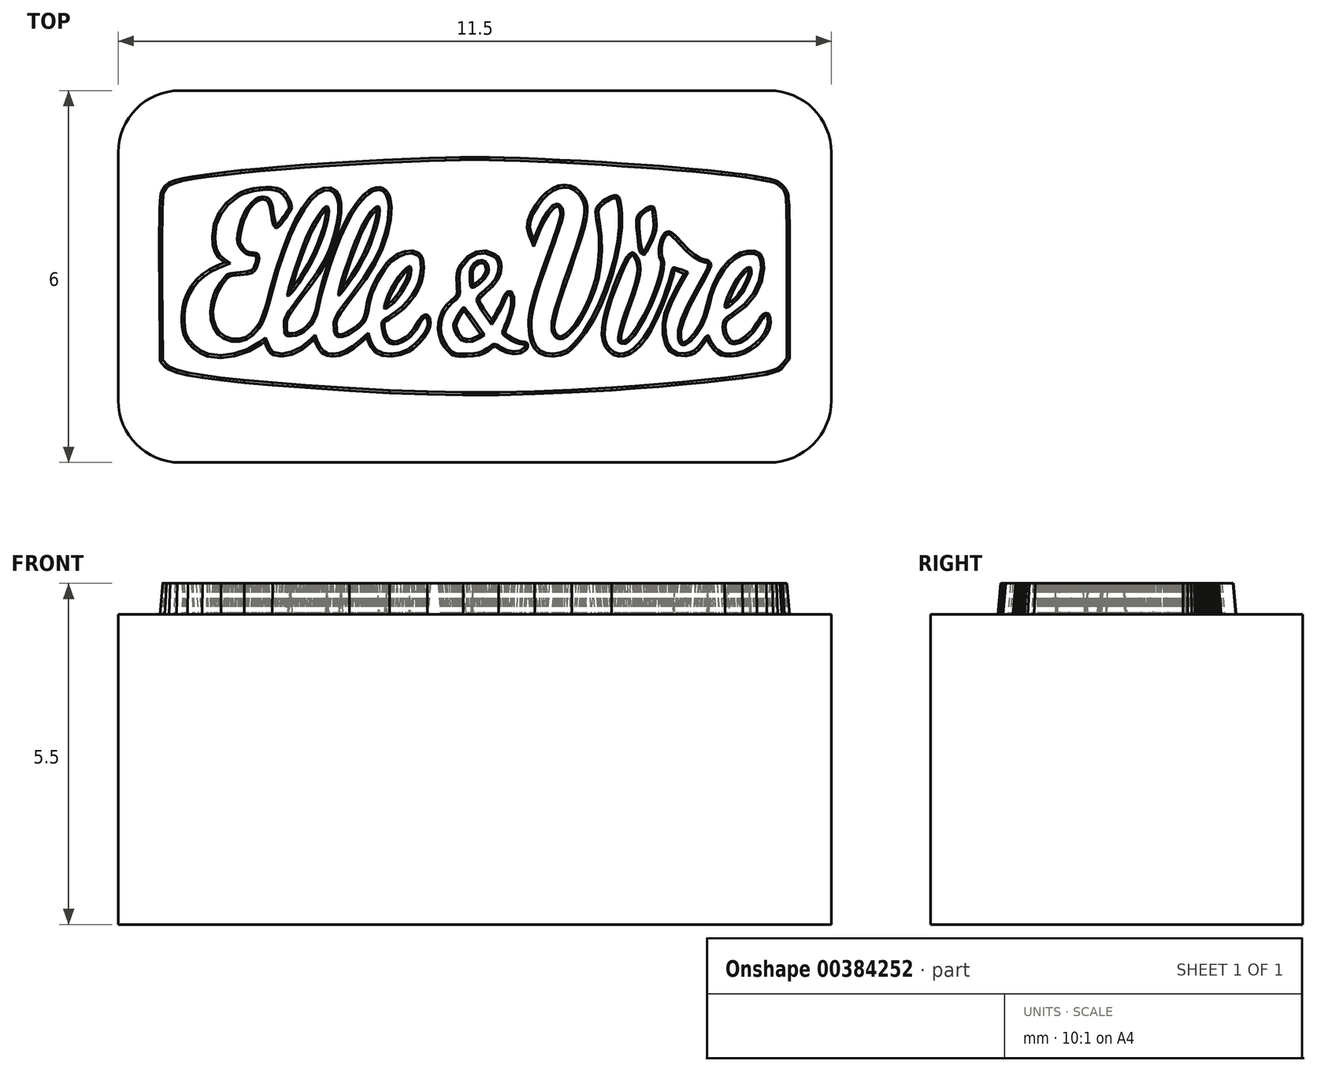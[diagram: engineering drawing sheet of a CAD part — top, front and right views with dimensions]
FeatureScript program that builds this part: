
annotation { "Feature Type Name" : "Feature", "Feature Type Description" : "" }
export const myFeature = defineFeature(function(context is Context, id is Id, definition is map)
    precondition{}
    {
        {
            var Q0;
            Q0=qCreatedBy(makeId("Top.planeOp"),FACE);
            var sketch = newSketch(context, id + "F0", { "sketchPlane" : qUnion([Q0])});
            skLineSegment(sketch, "E0.bottom", {"start": v(-4.75, 3) * mm, "end": v(4.75, 3) * mm});
            skLineSegment(sketch, "E0.top", {"start": v(-4.75, -3) * mm, "end": v(4.75, -3) * mm});
            skLineSegment(sketch, "E0.left", {"start": v(-5.75, 2) * mm, "end": v(-5.75, -2) * mm});
            skLineSegment(sketch, "E0.right", {"start": v(5.75, 2) * mm, "end": v(5.75, -2) * mm});
            skLineSegment(sketch, "E1", {"start": v(-5.75, 0) * mm, "end": v(5.75, 0) * mm});
            skPoint(sketch, "E2.visualSharp", {"position": v(-5.75, 3) * mm});
            skArc(sketch, "E2.filletArc", {"start": v(-4.75, 3) * mm, "mid": v(-5.46, 2.7) * mm, "end": v(-5.75, 2) * mm});
            skPoint(sketch, "E3.visualSharp", {"position": v(-5.75, -3) * mm});
            skArc(sketch, "E3.filletArc", {"start": v(-5.75, -2) * mm, "mid": v(-5.46, -2.7) * mm, "end": v(-4.75, -3) * mm});
            skPoint(sketch, "E4.visualSharp", {"position": v(5.75, 3) * mm});
            skArc(sketch, "E4.filletArc", {"start": v(5.75, 2) * mm, "mid": v(5.46, 2.7) * mm, "end": v(4.75, 3) * mm});
            skPoint(sketch, "E5.visualSharp", {"position": v(5.75, -3) * mm});
            skArc(sketch, "E5.filletArc", {"start": v(4.75, -3) * mm, "mid": v(5.46, -2.7) * mm, "end": v(5.75, -2) * mm});
            skSolve(sketch);
        }
        {
            var Q0;
            Q0=qCreatedBy(makeId("Top.planeOp"),FACE);
            var sketch = newSketch(context, id + "F1", { "sketchPlane" : qUnion([Q0])});
            skLineSegment(sketch, "E6", {"start": v(-1.14, -2.45) * mm, "end": v(-1.5, -2.42) * mm});
            skLineSegment(sketch, "E7", {"start": v(-1.5, -2.42) * mm, "end": v(-1.84, -2.39) * mm});
            skLineSegment(sketch, "E8", {"start": v(-1.84, -2.39) * mm, "end": v(-2.17, -2.34) * mm});
            skLineSegment(sketch, "E9", {"start": v(-2.17, -2.34) * mm, "end": v(-2.5, -2.3) * mm});
            skLineSegment(sketch, "E10", {"start": v(-2.5, -2.3) * mm, "end": v(-2.81, -2.25) * mm});
            skLineSegment(sketch, "E11", {"start": v(-2.81, -2.25) * mm, "end": v(-3.11, -2.2) * mm});
            skLineSegment(sketch, "E12", {"start": v(-3.11, -2.2) * mm, "end": v(-3.4, -2.14) * mm});
            skLineSegment(sketch, "E13", {"start": v(-3.4, -2.14) * mm, "end": v(-3.67, -2.08) * mm});
            skLineSegment(sketch, "E14", {"start": v(-3.67, -2.08) * mm, "end": v(-3.92, -2.01) * mm});
            skLineSegment(sketch, "E15", {"start": v(-3.92, -2.01) * mm, "end": v(-4.15, -1.95) * mm});
            skLineSegment(sketch, "E16", {"start": v(-4.15, -1.95) * mm, "end": v(-4.36, -1.89) * mm});
            skLineSegment(sketch, "E17", {"start": v(-4.36, -1.89) * mm, "end": v(-4.54, -1.82) * mm});
            skLineSegment(sketch, "E18", {"start": v(-4.54, -1.82) * mm, "end": v(-4.7, -1.75) * mm});
            skLineSegment(sketch, "E19", {"start": v(-4.7, -1.75) * mm, "end": v(-4.84, -1.68) * mm});
            skLineSegment(sketch, "E20", {"start": v(-4.84, -1.68) * mm, "end": v(-4.94, -1.62) * mm});
            skLineSegment(sketch, "E21", {"start": v(-4.94, -1.62) * mm, "end": v(-5.01, -1.55) * mm});
            skLineSegment(sketch, "E22", {"start": v(-5.01, -1.55) * mm, "end": v(-5.1, -1.44) * mm});
            skLineSegment(sketch, "E23", {"start": v(-5.1, -1.44) * mm, "end": v(-5.1, 1.43) * mm});
            skLineSegment(sketch, "E24", {"start": v(-5.1, 1.43) * mm, "end": v(-5.04, 1.53) * mm});
            skLineSegment(sketch, "E25", {"start": v(-5.04, 1.53) * mm, "end": v(-4.98, 1.6) * mm});
            skLineSegment(sketch, "E26", {"start": v(-4.98, 1.6) * mm, "end": v(-4.9, 1.65) * mm});
            skLineSegment(sketch, "E27", {"start": v(-4.9, 1.65) * mm, "end": v(-4.8, 1.71) * mm});
            skLineSegment(sketch, "E28", {"start": v(-4.8, 1.71) * mm, "end": v(-4.66, 1.78) * mm});
            skLineSegment(sketch, "E29", {"start": v(-4.66, 1.78) * mm, "end": v(-4.51, 1.84) * mm});
            skLineSegment(sketch, "E30", {"start": v(-4.51, 1.84) * mm, "end": v(-4.34, 1.9) * mm});
            skLineSegment(sketch, "E31", {"start": v(-4.34, 1.9) * mm, "end": v(-4.15, 1.96) * mm});
            skLineSegment(sketch, "E32", {"start": v(-4.15, 1.96) * mm, "end": v(-3.94, 2.02) * mm});
            skLineSegment(sketch, "E33", {"start": v(-3.94, 2.02) * mm, "end": v(-3.71, 2.08) * mm});
            skLineSegment(sketch, "E34", {"start": v(-3.71, 2.08) * mm, "end": v(-3.47, 2.13) * mm});
            skLineSegment(sketch, "E35", {"start": v(-3.47, 2.13) * mm, "end": v(-3.21, 2.18) * mm});
            skLineSegment(sketch, "E36", {"start": v(-3.21, 2.18) * mm, "end": v(-2.94, 2.23) * mm});
            skLineSegment(sketch, "E37", {"start": v(-2.94, 2.23) * mm, "end": v(-2.65, 2.28) * mm});
            skLineSegment(sketch, "E38", {"start": v(-2.65, 2.28) * mm, "end": v(-2.35, 2.33) * mm});
            skLineSegment(sketch, "E39", {"start": v(-2.35, 2.33) * mm, "end": v(-2.03, 2.37) * mm});
            skLineSegment(sketch, "E40", {"start": v(-2.03, 2.37) * mm, "end": v(-1.71, 2.4) * mm});
            skLineSegment(sketch, "E41", {"start": v(-1.71, 2.4) * mm, "end": v(-1.57, 2.42) * mm});
            skLineSegment(sketch, "E42", {"start": v(-1.57, 2.42) * mm, "end": v(-1.4, 2.44) * mm});
            skLineSegment(sketch, "E43", {"start": v(-1.4, 2.44) * mm, "end": v(-1.2, 2.45) * mm});
            skLineSegment(sketch, "E44", {"start": v(-1.2, 2.45) * mm, "end": v(-1, 2.46) * mm});
            skLineSegment(sketch, "E45", {"start": v(-1, 2.46) * mm, "end": v(-0.79, 2.46) * mm});
            skLineSegment(sketch, "E46", {"start": v(-0.79, 2.46) * mm, "end": v(-0.56, 2.47) * mm});
            skLineSegment(sketch, "E47", {"start": v(-0.56, 2.47) * mm, "end": v(-0.33, 2.47) * mm});
            skLineSegment(sketch, "E48", {"start": v(-0.33, 2.47) * mm, "end": v(-0.1, 2.48) * mm});
            skLineSegment(sketch, "E49", {"start": v(-0.1, 2.48) * mm, "end": v(0.14, 2.48) * mm});
            skLineSegment(sketch, "E50", {"start": v(0.14, 2.48) * mm, "end": v(0.38, 2.48) * mm});
            skLineSegment(sketch, "E51", {"start": v(0.38, 2.48) * mm, "end": v(0.6, 2.47) * mm});
            skLineSegment(sketch, "E52", {"start": v(0.6, 2.47) * mm, "end": v(0.82, 2.47) * mm});
            skLineSegment(sketch, "E53", {"start": v(0.82, 2.47) * mm, "end": v(1.02, 2.46) * mm});
            skLineSegment(sketch, "E54", {"start": v(1.02, 2.46) * mm, "end": v(1.2, 2.45) * mm});
            skLineSegment(sketch, "E55", {"start": v(1.2, 2.45) * mm, "end": v(1.37, 2.44) * mm});
            skLineSegment(sketch, "E56", {"start": v(1.37, 2.44) * mm, "end": v(1.5, 2.43) * mm});
            skLineSegment(sketch, "E57", {"start": v(1.5, 2.43) * mm, "end": v(1.94, 2.38) * mm});
            skLineSegment(sketch, "E58", {"start": v(1.94, 2.38) * mm, "end": v(2.35, 2.33) * mm});
            skLineSegment(sketch, "E59", {"start": v(2.35, 2.33) * mm, "end": v(2.75, 2.26) * mm});
            skLineSegment(sketch, "E60", {"start": v(2.75, 2.26) * mm, "end": v(3.13, 2.2) * mm});
            skLineSegment(sketch, "E61", {"start": v(3.13, 2.2) * mm, "end": v(3.48, 2.13) * mm});
            skLineSegment(sketch, "E62", {"start": v(3.48, 2.13) * mm, "end": v(3.8, 2.05) * mm});
            skLineSegment(sketch, "E63", {"start": v(3.8, 2.05) * mm, "end": v(4.09, 1.98) * mm});
            skLineSegment(sketch, "E64", {"start": v(4.09, 1.98) * mm, "end": v(4.34, 1.9) * mm});
            skLineSegment(sketch, "E65", {"start": v(4.34, 1.9) * mm, "end": v(4.61, 1.8) * mm});
            skLineSegment(sketch, "E66", {"start": v(4.61, 1.8) * mm, "end": v(4.8, 1.7) * mm});
            skLineSegment(sketch, "E67", {"start": v(4.8, 1.7) * mm, "end": v(4.95, 1.6) * mm});
            skLineSegment(sketch, "E68", {"start": v(4.95, 1.6) * mm, "end": v(5.03, 1.5) * mm});
            skLineSegment(sketch, "E69", {"start": v(5.03, 1.5) * mm, "end": v(5.1, 1.4) * mm});
            skLineSegment(sketch, "E70", {"start": v(5.1, 1.4) * mm, "end": v(5.1, 0) * mm});
            skLineSegment(sketch, "E71", {"start": v(5.1, 0) * mm, "end": v(5.1, -0.23) * mm});
            skLineSegment(sketch, "E72", {"start": v(5.1, -0.23) * mm, "end": v(5.1, -0.45) * mm});
            skLineSegment(sketch, "E73", {"start": v(5.1, -0.45) * mm, "end": v(5.1, -0.63) * mm});
            skLineSegment(sketch, "E74", {"start": v(5.1, -0.63) * mm, "end": v(5.1, -0.79) * mm});
            skLineSegment(sketch, "E75", {"start": v(5.1, -0.79) * mm, "end": v(5.1, -0.92) * mm});
            skLineSegment(sketch, "E76", {"start": v(5.1, -0.92) * mm, "end": v(5.1, -1.04) * mm});
            skLineSegment(sketch, "E77", {"start": v(5.1, -1.04) * mm, "end": v(5.1, -1.13) * mm});
            skLineSegment(sketch, "E78", {"start": v(5.1, -1.13) * mm, "end": v(5.1, -1.21) * mm});
            skLineSegment(sketch, "E79", {"start": v(5.1, -1.21) * mm, "end": v(5.1, -1.28) * mm});
            skLineSegment(sketch, "E80", {"start": v(5.1, -1.28) * mm, "end": v(5.1, -1.33) * mm});
            skLineSegment(sketch, "E81", {"start": v(5.1, -1.33) * mm, "end": v(5.09, -1.37) * mm});
            skLineSegment(sketch, "E82", {"start": v(5.09, -1.37) * mm, "end": v(5.08, -1.4) * mm});
            skLineSegment(sketch, "E83", {"start": v(5.08, -1.4) * mm, "end": v(5.07, -1.43) * mm});
            skLineSegment(sketch, "E84", {"start": v(5.07, -1.43) * mm, "end": v(5.06, -1.45) * mm});
            skLineSegment(sketch, "E85", {"start": v(5.06, -1.45) * mm, "end": v(5.06, -1.47) * mm});
            skLineSegment(sketch, "E86", {"start": v(5.06, -1.47) * mm, "end": v(5.05, -1.49) * mm});
            skLineSegment(sketch, "E87", {"start": v(5.05, -1.49) * mm, "end": v(5.01, -1.53) * mm});
            skLineSegment(sketch, "E88", {"start": v(5.01, -1.53) * mm, "end": v(4.97, -1.58) * mm});
            skLineSegment(sketch, "E89", {"start": v(4.97, -1.58) * mm, "end": v(4.92, -1.63) * mm});
            skLineSegment(sketch, "E90", {"start": v(4.92, -1.63) * mm, "end": v(4.87, -1.66) * mm});
            skLineSegment(sketch, "E91", {"start": v(4.87, -1.66) * mm, "end": v(4.68, -1.77) * mm});
            skLineSegment(sketch, "E92", {"start": v(4.68, -1.77) * mm, "end": v(4.4, -1.87) * mm});
            skLineSegment(sketch, "E93", {"start": v(4.4, -1.87) * mm, "end": v(4.05, -1.98) * mm});
            skLineSegment(sketch, "E94", {"start": v(4.05, -1.98) * mm, "end": v(3.65, -2.08) * mm});
            skLineSegment(sketch, "E95", {"start": v(3.65, -2.08) * mm, "end": v(3.2, -2.17) * mm});
            skLineSegment(sketch, "E96", {"start": v(3.2, -2.17) * mm, "end": v(2.72, -2.26) * mm});
            skLineSegment(sketch, "E97", {"start": v(2.72, -2.26) * mm, "end": v(2.22, -2.34) * mm});
            skLineSegment(sketch, "E98", {"start": v(2.22, -2.34) * mm, "end": v(1.7, -2.4) * mm});
            skLineSegment(sketch, "E99", {"start": v(1.7, -2.4) * mm, "end": v(1.4, -2.43) * mm});
            skLineSegment(sketch, "E100", {"start": v(1.4, -2.43) * mm, "end": v(1.05, -2.45) * mm});
            skLineSegment(sketch, "E101", {"start": v(1.05, -2.45) * mm, "end": v(0.66, -2.46) * mm});
            skLineSegment(sketch, "E102", {"start": v(0.66, -2.46) * mm, "end": v(0.24, -2.47) * mm});
            skLineSegment(sketch, "E103", {"start": v(0.24, -2.47) * mm, "end": v(-0.17, -2.48) * mm});
            skLineSegment(sketch, "E104", {"start": v(-0.17, -2.48) * mm, "end": v(-0.55, -2.48) * mm});
            skLineSegment(sketch, "E105", {"start": v(-0.55, -2.48) * mm, "end": v(-0.88, -2.47) * mm});
            skLineSegment(sketch, "E106", {"start": v(-0.88, -2.47) * mm, "end": v(-1.14, -2.45) * mm});
            skLineSegment(sketch, "E107", {"start": v(2.2, -1.83) * mm, "end": v(2.58, -1.8) * mm});
            skLineSegment(sketch, "E108", {"start": v(2.58, -1.8) * mm, "end": v(2.97, -1.78) * mm});
            skLineSegment(sketch, "E109", {"start": v(2.97, -1.78) * mm, "end": v(3.35, -1.74) * mm});
            skLineSegment(sketch, "E110", {"start": v(3.35, -1.74) * mm, "end": v(3.7, -1.7) * mm});
            skLineSegment(sketch, "E111", {"start": v(3.7, -1.7) * mm, "end": v(4.04, -1.67) * mm});
            skLineSegment(sketch, "E112", {"start": v(4.04, -1.67) * mm, "end": v(4.32, -1.64) * mm});
            skLineSegment(sketch, "E113", {"start": v(4.32, -1.64) * mm, "end": v(4.55, -1.6) * mm});
            skLineSegment(sketch, "E114", {"start": v(4.55, -1.6) * mm, "end": v(4.71, -1.58) * mm});
            skLineSegment(sketch, "E115", {"start": v(4.71, -1.58) * mm, "end": v(4.81, -1.55) * mm});
            skLineSegment(sketch, "E116", {"start": v(4.81, -1.55) * mm, "end": v(4.9, -1.52) * mm});
            skLineSegment(sketch, "E117", {"start": v(4.9, -1.52) * mm, "end": v(4.95, -1.48) * mm});
            skLineSegment(sketch, "E118", {"start": v(4.95, -1.48) * mm, "end": v(5, -1.43) * mm});
            skLineSegment(sketch, "E119", {"start": v(5, -1.43) * mm, "end": v(5.08, -1.33) * mm});
            skLineSegment(sketch, "E120", {"start": v(5.08, -1.33) * mm, "end": v(5.08, 0) * mm});
            skLineSegment(sketch, "E121", {"start": v(5.08, 0) * mm, "end": v(5.08, 0.22) * mm});
            skLineSegment(sketch, "E122", {"start": v(5.08, 0.22) * mm, "end": v(5.08, 0.42) * mm});
            skLineSegment(sketch, "E123", {"start": v(5.08, 0.42) * mm, "end": v(5.08, 0.6) * mm});
            skLineSegment(sketch, "E124", {"start": v(5.08, 0.6) * mm, "end": v(5.08, 0.74) * mm});
            skLineSegment(sketch, "E125", {"start": v(5.08, 0.74) * mm, "end": v(5.07, 0.87) * mm});
            skLineSegment(sketch, "E126", {"start": v(5.07, 0.87) * mm, "end": v(5.07, 0.98) * mm});
            skLineSegment(sketch, "E127", {"start": v(5.07, 0.98) * mm, "end": v(5.07, 1.07) * mm});
            skLineSegment(sketch, "E128", {"start": v(5.07, 1.07) * mm, "end": v(5.07, 1.15) * mm});
            skLineSegment(sketch, "E129", {"start": v(5.07, 1.15) * mm, "end": v(5.07, 1.2) * mm});
            skLineSegment(sketch, "E130", {"start": v(5.07, 1.2) * mm, "end": v(5.06, 1.26) * mm});
            skLineSegment(sketch, "E131", {"start": v(5.06, 1.26) * mm, "end": v(5.06, 1.3) * mm});
            skLineSegment(sketch, "E132", {"start": v(5.06, 1.3) * mm, "end": v(5.05, 1.33) * mm});
            skLineSegment(sketch, "E133", {"start": v(5.05, 1.33) * mm, "end": v(5.04, 1.36) * mm});
            skLineSegment(sketch, "E134", {"start": v(5.04, 1.36) * mm, "end": v(5.04, 1.38) * mm});
            skLineSegment(sketch, "E135", {"start": v(5.04, 1.38) * mm, "end": v(5.03, 1.4) * mm});
            skLineSegment(sketch, "E136", {"start": v(5.03, 1.4) * mm, "end": v(5.02, 1.41) * mm});
            skLineSegment(sketch, "E137", {"start": v(5.02, 1.41) * mm, "end": v(4.99, 1.46) * mm});
            skLineSegment(sketch, "E138", {"start": v(4.99, 1.46) * mm, "end": v(4.94, 1.5) * mm});
            skLineSegment(sketch, "E139", {"start": v(4.94, 1.5) * mm, "end": v(4.9, 1.53) * mm});
            skLineSegment(sketch, "E140", {"start": v(4.9, 1.53) * mm, "end": v(4.85, 1.55) * mm});
            skLineSegment(sketch, "E141", {"start": v(4.85, 1.55) * mm, "end": v(4.77, 1.57) * mm});
            skLineSegment(sketch, "E142", {"start": v(4.77, 1.57) * mm, "end": v(4.66, 1.6) * mm});
            skLineSegment(sketch, "E143", {"start": v(4.66, 1.6) * mm, "end": v(4.53, 1.62) * mm});
            skLineSegment(sketch, "E144", {"start": v(4.53, 1.62) * mm, "end": v(4.37, 1.64) * mm});
            skLineSegment(sketch, "E145", {"start": v(4.37, 1.64) * mm, "end": v(4.19, 1.67) * mm});
            skLineSegment(sketch, "E146", {"start": v(4.19, 1.67) * mm, "end": v(3.98, 1.69) * mm});
            skLineSegment(sketch, "E147", {"start": v(3.98, 1.69) * mm, "end": v(3.76, 1.71) * mm});
            skLineSegment(sketch, "E148", {"start": v(3.76, 1.71) * mm, "end": v(3.52, 1.74) * mm});
            skLineSegment(sketch, "E149", {"start": v(3.52, 1.74) * mm, "end": v(3.25, 1.76) * mm});
            skLineSegment(sketch, "E150", {"start": v(3.25, 1.76) * mm, "end": v(2.97, 1.78) * mm});
            skLineSegment(sketch, "E151", {"start": v(2.97, 1.78) * mm, "end": v(2.68, 1.8) * mm});
            skLineSegment(sketch, "E152", {"start": v(2.68, 1.8) * mm, "end": v(2.37, 1.82) * mm});
            skLineSegment(sketch, "E153", {"start": v(2.37, 1.82) * mm, "end": v(2.05, 1.84) * mm});
            skLineSegment(sketch, "E154", {"start": v(2.05, 1.84) * mm, "end": v(1.71, 1.86) * mm});
            skLineSegment(sketch, "E155", {"start": v(1.71, 1.86) * mm, "end": v(1.37, 1.88) * mm});
            skLineSegment(sketch, "E156", {"start": v(1.37, 1.88) * mm, "end": v(1.02, 1.9) * mm});
            skLineSegment(sketch, "E157", {"start": v(1.02, 1.9) * mm, "end": v(0.73, 1.91) * mm});
            skLineSegment(sketch, "E158", {"start": v(0.73, 1.91) * mm, "end": v(0.47, 1.92) * mm});
            skLineSegment(sketch, "E159", {"start": v(0.47, 1.92) * mm, "end": v(0.23, 1.92) * mm});
            skLineSegment(sketch, "E160", {"start": v(0.23, 1.92) * mm, "end": v(0, 1.93) * mm});
            skLineSegment(sketch, "E161", {"start": v(0, 1.93) * mm, "end": v(-0.23, 1.92) * mm});
            skLineSegment(sketch, "E162", {"start": v(-0.23, 1.92) * mm, "end": v(-0.48, 1.92) * mm});
            skLineSegment(sketch, "E163", {"start": v(-0.48, 1.92) * mm, "end": v(-0.74, 1.91) * mm});
            skLineSegment(sketch, "E164", {"start": v(-0.74, 1.91) * mm, "end": v(-1.02, 1.9) * mm});
            skLineSegment(sketch, "E165", {"start": v(-1.02, 1.9) * mm, "end": v(-1.48, 1.88) * mm});
            skLineSegment(sketch, "E166", {"start": v(-1.48, 1.88) * mm, "end": v(-1.92, 1.85) * mm});
            skLineSegment(sketch, "E167", {"start": v(-1.92, 1.85) * mm, "end": v(-2.34, 1.83) * mm});
            skLineSegment(sketch, "E168", {"start": v(-2.34, 1.83) * mm, "end": v(-2.75, 1.8) * mm});
            skLineSegment(sketch, "E169", {"start": v(-2.75, 1.8) * mm, "end": v(-3.12, 1.77) * mm});
            skLineSegment(sketch, "E170", {"start": v(-3.12, 1.77) * mm, "end": v(-3.47, 1.74) * mm});
            skLineSegment(sketch, "E171", {"start": v(-3.47, 1.74) * mm, "end": v(-3.77, 1.71) * mm});
            skLineSegment(sketch, "E172", {"start": v(-3.77, 1.71) * mm, "end": v(-4.04, 1.68) * mm});
            skLineSegment(sketch, "E173", {"start": v(-4.04, 1.68) * mm, "end": v(-4.33, 1.65) * mm});
            skLineSegment(sketch, "E174", {"start": v(-4.33, 1.65) * mm, "end": v(-4.55, 1.61) * mm});
            skLineSegment(sketch, "E175", {"start": v(-4.55, 1.61) * mm, "end": v(-4.72, 1.58) * mm});
            skLineSegment(sketch, "E176", {"start": v(-4.72, 1.58) * mm, "end": v(-4.85, 1.55) * mm});
            skLineSegment(sketch, "E177", {"start": v(-4.85, 1.55) * mm, "end": v(-4.94, 1.5) * mm});
            skLineSegment(sketch, "E178", {"start": v(-4.94, 1.5) * mm, "end": v(-5, 1.46) * mm});
            skLineSegment(sketch, "E179", {"start": v(-5, 1.46) * mm, "end": v(-5.04, 1.4) * mm});
            skLineSegment(sketch, "E180", {"start": v(-5.04, 1.4) * mm, "end": v(-5.06, 1.34) * mm});
            skLineSegment(sketch, "E181", {"start": v(-5.06, 1.34) * mm, "end": v(-5.07, 1.3) * mm});
            skLineSegment(sketch, "E182", {"start": v(-5.07, 1.3) * mm, "end": v(-5.08, 1.2) * mm});
            skLineSegment(sketch, "E183", {"start": v(-5.08, 1.2) * mm, "end": v(-5.08, 1.08) * mm});
            skLineSegment(sketch, "E184", {"start": v(-5.08, 1.08) * mm, "end": v(-5.08, 0.91) * mm});
            skLineSegment(sketch, "E185", {"start": v(-5.08, 0.91) * mm, "end": v(-5.09, 0.71) * mm});
            skLineSegment(sketch, "E186", {"start": v(-5.09, 0.71) * mm, "end": v(-5.09, 0.48) * mm});
            skLineSegment(sketch, "E187", {"start": v(-5.09, 0.48) * mm, "end": v(-5.09, 0.22) * mm});
            skLineSegment(sketch, "E188", {"start": v(-5.09, 0.22) * mm, "end": v(-5.09, -0.06) * mm});
            skLineSegment(sketch, "E189", {"start": v(-5.09, -0.06) * mm, "end": v(-5.08, -1.37) * mm});
            skLineSegment(sketch, "E190", {"start": v(-5.08, -1.37) * mm, "end": v(-5, -1.45) * mm});
            skLineSegment(sketch, "E191", {"start": v(-5, -1.45) * mm, "end": v(-4.93, -1.5) * mm});
            skLineSegment(sketch, "E192", {"start": v(-4.93, -1.5) * mm, "end": v(-4.81, -1.55) * mm});
            skLineSegment(sketch, "E193", {"start": v(-4.81, -1.55) * mm, "end": v(-4.63, -1.6) * mm});
            skLineSegment(sketch, "E194", {"start": v(-4.63, -1.6) * mm, "end": v(-4.4, -1.63) * mm});
            skLineSegment(sketch, "E195", {"start": v(-4.4, -1.63) * mm, "end": v(-4.1, -1.67) * mm});
            skLineSegment(sketch, "E196", {"start": v(-4.1, -1.67) * mm, "end": v(-3.72, -1.71) * mm});
            skLineSegment(sketch, "E197", {"start": v(-3.72, -1.71) * mm, "end": v(-3.27, -1.75) * mm});
            skLineSegment(sketch, "E198", {"start": v(-3.27, -1.75) * mm, "end": v(-2.73, -1.8) * mm});
            skLineSegment(sketch, "E199", {"start": v(-2.73, -1.8) * mm, "end": v(-2.02, -1.84) * mm});
            skLineSegment(sketch, "E200", {"start": v(-2.02, -1.84) * mm, "end": v(-1.37, -1.88) * mm});
            skLineSegment(sketch, "E201", {"start": v(-1.37, -1.88) * mm, "end": v(-0.77, -1.9) * mm});
            skLineSegment(sketch, "E202", {"start": v(-0.77, -1.9) * mm, "end": v(-0.18, -1.91) * mm});
            skLineSegment(sketch, "E203", {"start": v(-0.18, -1.91) * mm, "end": v(0.39, -1.9) * mm});
            skLineSegment(sketch, "E204", {"start": v(0.39, -1.9) * mm, "end": v(0.97, -1.9) * mm});
            skLineSegment(sketch, "E205", {"start": v(0.97, -1.9) * mm, "end": v(1.57, -1.87) * mm});
            skLineSegment(sketch, "E206", {"start": v(1.57, -1.87) * mm, "end": v(2.2, -1.83) * mm});
            skLineSegment(sketch, "E207", {"start": v(-4.3, -1.24) * mm, "end": v(-4.41, -1.2) * mm});
            skLineSegment(sketch, "E208", {"start": v(-4.41, -1.2) * mm, "end": v(-4.52, -1.12) * mm});
            skLineSegment(sketch, "E209", {"start": v(-4.52, -1.12) * mm, "end": v(-4.6, -1.02) * mm});
            skLineSegment(sketch, "E210", {"start": v(-4.6, -1.02) * mm, "end": v(-4.66, -0.92) * mm});
            skLineSegment(sketch, "E211", {"start": v(-4.66, -0.92) * mm, "end": v(-4.67, -0.87) * mm});
            skLineSegment(sketch, "E212", {"start": v(-4.67, -0.87) * mm, "end": v(-4.68, -0.8) * mm});
            skLineSegment(sketch, "E213", {"start": v(-4.68, -0.8) * mm, "end": v(-4.68, -0.72) * mm});
            skLineSegment(sketch, "E214", {"start": v(-4.68, -0.72) * mm, "end": v(-4.68, -0.65) * mm});
            skLineSegment(sketch, "E215", {"start": v(-4.68, -0.65) * mm, "end": v(-4.67, -0.52) * mm});
            skLineSegment(sketch, "E216", {"start": v(-4.67, -0.52) * mm, "end": v(-4.65, -0.4) * mm});
            skLineSegment(sketch, "E217", {"start": v(-4.65, -0.4) * mm, "end": v(-4.6, -0.28) * mm});
            skLineSegment(sketch, "E218", {"start": v(-4.6, -0.28) * mm, "end": v(-4.54, -0.18) * mm});
            skLineSegment(sketch, "E219", {"start": v(-4.54, -0.18) * mm, "end": v(-4.46, -0.08) * mm});
            skLineSegment(sketch, "E220", {"start": v(-4.46, -0.08) * mm, "end": v(-4.37, 0) * mm});
            skLineSegment(sketch, "E221", {"start": v(-4.37, 0) * mm, "end": v(-4.26, 0.08) * mm});
            skLineSegment(sketch, "E222", {"start": v(-4.26, 0.08) * mm, "end": v(-4.14, 0.14) * mm});
            skLineSegment(sketch, "E223", {"start": v(-4.14, 0.14) * mm, "end": v(-3.94, 0.22) * mm});
            skLineSegment(sketch, "E224", {"start": v(-3.94, 0.22) * mm, "end": v(-4.04, 0.28) * mm});
            skLineSegment(sketch, "E225", {"start": v(-4.04, 0.28) * mm, "end": v(-4.1, 0.34) * mm});
            skLineSegment(sketch, "E226", {"start": v(-4.1, 0.34) * mm, "end": v(-4.16, 0.42) * mm});
            skLineSegment(sketch, "E227", {"start": v(-4.16, 0.42) * mm, "end": v(-4.18, 0.51) * mm});
            skLineSegment(sketch, "E228", {"start": v(-4.18, 0.51) * mm, "end": v(-4.19, 0.64) * mm});
            skLineSegment(sketch, "E229", {"start": v(-4.19, 0.64) * mm, "end": v(-4.16, 0.83) * mm});
            skLineSegment(sketch, "E230", {"start": v(-4.16, 0.83) * mm, "end": v(-4.1, 1) * mm});
            skLineSegment(sketch, "E231", {"start": v(-4.1, 1) * mm, "end": v(-3.98, 1.16) * mm});
            skLineSegment(sketch, "E232", {"start": v(-3.98, 1.16) * mm, "end": v(-3.8, 1.29) * mm});
            skLineSegment(sketch, "E233", {"start": v(-3.8, 1.29) * mm, "end": v(-3.74, 1.33) * mm});
            skLineSegment(sketch, "E234", {"start": v(-3.74, 1.33) * mm, "end": v(-3.66, 1.36) * mm});
            skLineSegment(sketch, "E235", {"start": v(-3.66, 1.36) * mm, "end": v(-3.56, 1.38) * mm});
            skLineSegment(sketch, "E236", {"start": v(-3.56, 1.38) * mm, "end": v(-3.47, 1.4) * mm});
            skLineSegment(sketch, "E237", {"start": v(-3.47, 1.4) * mm, "end": v(-3.37, 1.4) * mm});
            skLineSegment(sketch, "E238", {"start": v(-3.37, 1.4) * mm, "end": v(-3.28, 1.4) * mm});
            skLineSegment(sketch, "E239", {"start": v(-3.28, 1.4) * mm, "end": v(-3.2, 1.39) * mm});
            skLineSegment(sketch, "E240", {"start": v(-3.2, 1.39) * mm, "end": v(-3.14, 1.37) * mm});
            skLineSegment(sketch, "E241", {"start": v(-3.14, 1.37) * mm, "end": v(-3.1, 1.32) * mm});
            skLineSegment(sketch, "E242", {"start": v(-3.1, 1.32) * mm, "end": v(-3.04, 1.26) * mm});
            skLineSegment(sketch, "E243", {"start": v(-3.04, 1.26) * mm, "end": v(-3, 1.18) * mm});
            skLineSegment(sketch, "E244", {"start": v(-3, 1.18) * mm, "end": v(-3, 1.12) * mm});
            skLineSegment(sketch, "E245", {"start": v(-3, 1.12) * mm, "end": v(-3, 1.1) * mm});
            skLineSegment(sketch, "E246", {"start": v(-3, 1.1) * mm, "end": v(-3.02, 1.06) * mm});
            skLineSegment(sketch, "E247", {"start": v(-3.02, 1.06) * mm, "end": v(-3.05, 1.01) * mm});
            skLineSegment(sketch, "E248", {"start": v(-3.05, 1.01) * mm, "end": v(-3.09, 0.96) * mm});
            skLineSegment(sketch, "E249", {"start": v(-3.09, 0.96) * mm, "end": v(-3.12, 0.92) * mm});
            skLineSegment(sketch, "E250", {"start": v(-3.12, 0.92) * mm, "end": v(-3.16, 0.87) * mm});
            skLineSegment(sketch, "E251", {"start": v(-3.16, 0.87) * mm, "end": v(-3.18, 0.84) * mm});
            skLineSegment(sketch, "E252", {"start": v(-3.18, 0.84) * mm, "end": v(-3.2, 0.83) * mm});
            skLineSegment(sketch, "E253", {"start": v(-3.2, 0.83) * mm, "end": v(-3.2, 0.85) * mm});
            skLineSegment(sketch, "E254", {"start": v(-3.2, 0.85) * mm, "end": v(-3.22, 0.88) * mm});
            skLineSegment(sketch, "E255", {"start": v(-3.22, 0.88) * mm, "end": v(-3.23, 0.93) * mm});
            skLineSegment(sketch, "E256", {"start": v(-3.23, 0.93) * mm, "end": v(-3.24, 0.99) * mm});
            skLineSegment(sketch, "E257", {"start": v(-3.24, 0.99) * mm, "end": v(-3.26, 1.14) * mm});
            skLineSegment(sketch, "E258", {"start": v(-3.26, 1.14) * mm, "end": v(-3.3, 1.23) * mm});
            skLineSegment(sketch, "E259", {"start": v(-3.3, 1.23) * mm, "end": v(-3.34, 1.28) * mm});
            skLineSegment(sketch, "E260", {"start": v(-3.34, 1.28) * mm, "end": v(-3.42, 1.29) * mm});
            skLineSegment(sketch, "E261", {"start": v(-3.42, 1.29) * mm, "end": v(-3.48, 1.28) * mm});
            skLineSegment(sketch, "E262", {"start": v(-3.48, 1.28) * mm, "end": v(-3.55, 1.24) * mm});
            skLineSegment(sketch, "E263", {"start": v(-3.55, 1.24) * mm, "end": v(-3.61, 1.18) * mm});
            skLineSegment(sketch, "E264", {"start": v(-3.61, 1.18) * mm, "end": v(-3.67, 1.1) * mm});
            skLineSegment(sketch, "E265", {"start": v(-3.67, 1.1) * mm, "end": v(-3.72, 1.02) * mm});
            skLineSegment(sketch, "E266", {"start": v(-3.72, 1.02) * mm, "end": v(-3.77, 0.91) * mm});
            skLineSegment(sketch, "E267", {"start": v(-3.77, 0.91) * mm, "end": v(-3.8, 0.8) * mm});
            skLineSegment(sketch, "E268", {"start": v(-3.8, 0.8) * mm, "end": v(-3.82, 0.68) * mm});
            skLineSegment(sketch, "E269", {"start": v(-3.82, 0.68) * mm, "end": v(-3.83, 0.6) * mm});
            skLineSegment(sketch, "E270", {"start": v(-3.83, 0.6) * mm, "end": v(-3.83, 0.54) * mm});
            skLineSegment(sketch, "E271", {"start": v(-3.83, 0.54) * mm, "end": v(-3.8, 0.5) * mm});
            skLineSegment(sketch, "E272", {"start": v(-3.8, 0.5) * mm, "end": v(-3.77, 0.44) * mm});
            skLineSegment(sketch, "E273", {"start": v(-3.77, 0.44) * mm, "end": v(-3.73, 0.4) * mm});
            skLineSegment(sketch, "E274", {"start": v(-3.73, 0.4) * mm, "end": v(-3.7, 0.37) * mm});
            skLineSegment(sketch, "E275", {"start": v(-3.7, 0.37) * mm, "end": v(-3.65, 0.35) * mm});
            skLineSegment(sketch, "E276", {"start": v(-3.65, 0.35) * mm, "end": v(-3.6, 0.34) * mm});
            skLineSegment(sketch, "E277", {"start": v(-3.6, 0.34) * mm, "end": v(-3.57, 0.34) * mm});
            skLineSegment(sketch, "E278", {"start": v(-3.57, 0.34) * mm, "end": v(-3.55, 0.34) * mm});
            skLineSegment(sketch, "E279", {"start": v(-3.55, 0.34) * mm, "end": v(-3.53, 0.33) * mm});
            skLineSegment(sketch, "E280", {"start": v(-3.53, 0.33) * mm, "end": v(-3.52, 0.31) * mm});
            skLineSegment(sketch, "E281", {"start": v(-3.52, 0.31) * mm, "end": v(-3.52, 0.3) * mm});
            skLineSegment(sketch, "E282", {"start": v(-3.52, 0.3) * mm, "end": v(-3.53, 0.26) * mm});
            skLineSegment(sketch, "E283", {"start": v(-3.53, 0.26) * mm, "end": v(-3.54, 0.23) * mm});
            skLineSegment(sketch, "E284", {"start": v(-3.54, 0.23) * mm, "end": v(-3.55, 0.18) * mm});
            skLineSegment(sketch, "E285", {"start": v(-3.55, 0.18) * mm, "end": v(-3.57, 0.13) * mm});
            skLineSegment(sketch, "E286", {"start": v(-3.57, 0.13) * mm, "end": v(-3.61, 0.1) * mm});
            skLineSegment(sketch, "E287", {"start": v(-3.61, 0.1) * mm, "end": v(-3.68, 0.08) * mm});
            skLineSegment(sketch, "E288", {"start": v(-3.68, 0.08) * mm, "end": v(-3.79, 0.07) * mm});
            skLineSegment(sketch, "E289", {"start": v(-3.79, 0.07) * mm, "end": v(-3.85, 0.07) * mm});
            skLineSegment(sketch, "E290", {"start": v(-3.85, 0.07) * mm, "end": v(-3.9, 0.06) * mm});
            skLineSegment(sketch, "E291", {"start": v(-3.9, 0.06) * mm, "end": v(-3.94, 0.05) * mm});
            skLineSegment(sketch, "E292", {"start": v(-3.94, 0.05) * mm, "end": v(-3.98, 0.04) * mm});
            skLineSegment(sketch, "E293", {"start": v(-3.98, 0.04) * mm, "end": v(-4, 0.02) * mm});
            skLineSegment(sketch, "E294", {"start": v(-4, 0.02) * mm, "end": v(-4.04, -0.01) * mm});
            skLineSegment(sketch, "E295", {"start": v(-4.04, -0.01) * mm, "end": v(-4.07, -0.05) * mm});
            skLineSegment(sketch, "E296", {"start": v(-4.07, -0.05) * mm, "end": v(-4.1, -0.1) * mm});
            skLineSegment(sketch, "E297", {"start": v(-4.1, -0.1) * mm, "end": v(-4.2, -0.25) * mm});
            skLineSegment(sketch, "E298", {"start": v(-4.2, -0.25) * mm, "end": v(-4.24, -0.4) * mm});
            skLineSegment(sketch, "E299", {"start": v(-4.24, -0.4) * mm, "end": v(-4.27, -0.56) * mm});
            skLineSegment(sketch, "E300", {"start": v(-4.27, -0.56) * mm, "end": v(-4.26, -0.7) * mm});
            skLineSegment(sketch, "E301", {"start": v(-4.26, -0.7) * mm, "end": v(-4.21, -0.83) * mm});
            skLineSegment(sketch, "E302", {"start": v(-4.21, -0.83) * mm, "end": v(-4.14, -0.93) * mm});
            skLineSegment(sketch, "E303", {"start": v(-4.14, -0.93) * mm, "end": v(-4.04, -1) * mm});
            skLineSegment(sketch, "E304", {"start": v(-4.04, -1) * mm, "end": v(-3.92, -1.05) * mm});
            skLineSegment(sketch, "E305", {"start": v(-3.92, -1.05) * mm, "end": v(-3.8, -1.05) * mm});
            skLineSegment(sketch, "E306", {"start": v(-3.8, -1.05) * mm, "end": v(-3.68, -1.02) * mm});
            skLineSegment(sketch, "E307", {"start": v(-3.68, -1.02) * mm, "end": v(-3.58, -0.95) * mm});
            skLineSegment(sketch, "E308", {"start": v(-3.58, -0.95) * mm, "end": v(-3.48, -0.84) * mm});
            skLineSegment(sketch, "E309", {"start": v(-3.48, -0.84) * mm, "end": v(-3.43, -0.75) * mm});
            skLineSegment(sketch, "E310", {"start": v(-3.43, -0.75) * mm, "end": v(-3.38, -0.63) * mm});
            skLineSegment(sketch, "E311", {"start": v(-3.38, -0.63) * mm, "end": v(-3.32, -0.47) * mm});
            skLineSegment(sketch, "E312", {"start": v(-3.32, -0.47) * mm, "end": v(-3.26, -0.23) * mm});
            skLineSegment(sketch, "E313", {"start": v(-3.26, -0.23) * mm, "end": v(-3.17, 0.1) * mm});
            skLineSegment(sketch, "E314", {"start": v(-3.17, 0.1) * mm, "end": v(-3.07, 0.4) * mm});
            skLineSegment(sketch, "E315", {"start": v(-3.07, 0.4) * mm, "end": v(-2.97, 0.66) * mm});
            skLineSegment(sketch, "E316", {"start": v(-2.97, 0.66) * mm, "end": v(-2.86, 0.9) * mm});
            skLineSegment(sketch, "E317", {"start": v(-2.86, 0.9) * mm, "end": v(-2.75, 1.08) * mm});
            skLineSegment(sketch, "E318", {"start": v(-2.75, 1.08) * mm, "end": v(-2.64, 1.23) * mm});
            skLineSegment(sketch, "E319", {"start": v(-2.64, 1.23) * mm, "end": v(-2.53, 1.33) * mm});
            skLineSegment(sketch, "E320", {"start": v(-2.53, 1.33) * mm, "end": v(-2.43, 1.38) * mm});
            skLineSegment(sketch, "E321", {"start": v(-2.43, 1.38) * mm, "end": v(-2.34, 1.39) * mm});
            skLineSegment(sketch, "E322", {"start": v(-2.34, 1.39) * mm, "end": v(-2.27, 1.35) * mm});
            skLineSegment(sketch, "E323", {"start": v(-2.27, 1.35) * mm, "end": v(-2.22, 1.28) * mm});
            skLineSegment(sketch, "E324", {"start": v(-2.22, 1.28) * mm, "end": v(-2.2, 1.17) * mm});
            skLineSegment(sketch, "E325", {"start": v(-2.2, 1.17) * mm, "end": v(-2.2, 1.03) * mm});
            skLineSegment(sketch, "E326", {"start": v(-2.2, 1.03) * mm, "end": v(-2.22, 0.86) * mm});
            skLineSegment(sketch, "E327", {"start": v(-2.22, 0.86) * mm, "end": v(-2.27, 0.67) * mm});
            skLineSegment(sketch, "E328", {"start": v(-2.27, 0.67) * mm, "end": v(-2.34, 0.46) * mm});
            skLineSegment(sketch, "E329", {"start": v(-2.34, 0.46) * mm, "end": v(-2.37, 0.38) * mm});
            skLineSegment(sketch, "E330", {"start": v(-2.37, 0.38) * mm, "end": v(-2.4, 0.3) * mm});
            skLineSegment(sketch, "E331", {"start": v(-2.4, 0.3) * mm, "end": v(-2.45, 0.23) * mm});
            skLineSegment(sketch, "E332", {"start": v(-2.45, 0.23) * mm, "end": v(-2.5, 0.15) * mm});
            skLineSegment(sketch, "E333", {"start": v(-2.5, 0.15) * mm, "end": v(-2.54, 0.07) * mm});
            skLineSegment(sketch, "E334", {"start": v(-2.54, 0.07) * mm, "end": v(-2.6, -0.02) * mm});
            skLineSegment(sketch, "E335", {"start": v(-2.6, -0.02) * mm, "end": v(-2.68, -0.12) * mm});
            skLineSegment(sketch, "E336", {"start": v(-2.68, -0.12) * mm, "end": v(-2.77, -0.24) * mm});
            skLineSegment(sketch, "E337", {"start": v(-2.77, -0.24) * mm, "end": v(-2.87, -0.38) * mm});
            skLineSegment(sketch, "E338", {"start": v(-2.87, -0.38) * mm, "end": v(-2.95, -0.48) * mm});
            skLineSegment(sketch, "E339", {"start": v(-2.95, -0.48) * mm, "end": v(-3, -0.56) * mm});
            skLineSegment(sketch, "E340", {"start": v(-3, -0.56) * mm, "end": v(-3.04, -0.62) * mm});
            skLineSegment(sketch, "E341", {"start": v(-3.04, -0.62) * mm, "end": v(-3.06, -0.67) * mm});
            skLineSegment(sketch, "E342", {"start": v(-3.06, -0.67) * mm, "end": v(-3.07, -0.72) * mm});
            skLineSegment(sketch, "E343", {"start": v(-3.07, -0.72) * mm, "end": v(-3.08, -0.76) * mm});
            skLineSegment(sketch, "E344", {"start": v(-3.08, -0.76) * mm, "end": v(-3.08, -0.81) * mm});
            skLineSegment(sketch, "E345", {"start": v(-3.08, -0.81) * mm, "end": v(-3.07, -0.86) * mm});
            skLineSegment(sketch, "E346", {"start": v(-3.07, -0.86) * mm, "end": v(-3.07, -0.9) * mm});
            skLineSegment(sketch, "E347", {"start": v(-3.07, -0.9) * mm, "end": v(-3.06, -0.92) * mm});
            skLineSegment(sketch, "E348", {"start": v(-3.06, -0.92) * mm, "end": v(-3.05, -0.94) * mm});
            skLineSegment(sketch, "E349", {"start": v(-3.05, -0.94) * mm, "end": v(-3.04, -0.95) * mm});
            skLineSegment(sketch, "E350", {"start": v(-3.04, -0.95) * mm, "end": v(-3.02, -0.96) * mm});
            skLineSegment(sketch, "E351", {"start": v(-3.02, -0.96) * mm, "end": v(-2.99, -0.96) * mm});
            skLineSegment(sketch, "E352", {"start": v(-2.99, -0.96) * mm, "end": v(-2.95, -0.96) * mm});
            skLineSegment(sketch, "E353", {"start": v(-2.95, -0.96) * mm, "end": v(-2.88, -0.95) * mm});
            skLineSegment(sketch, "E354", {"start": v(-2.88, -0.95) * mm, "end": v(-2.81, -0.92) * mm});
            skLineSegment(sketch, "E355", {"start": v(-2.81, -0.92) * mm, "end": v(-2.75, -0.88) * mm});
            skLineSegment(sketch, "E356", {"start": v(-2.75, -0.88) * mm, "end": v(-2.69, -0.83) * mm});
            skLineSegment(sketch, "E357", {"start": v(-2.69, -0.83) * mm, "end": v(-2.63, -0.77) * mm});
            skLineSegment(sketch, "E358", {"start": v(-2.63, -0.77) * mm, "end": v(-2.59, -0.7) * mm});
            skLineSegment(sketch, "E359", {"start": v(-2.59, -0.7) * mm, "end": v(-2.55, -0.63) * mm});
            skLineSegment(sketch, "E360", {"start": v(-2.55, -0.63) * mm, "end": v(-2.53, -0.55) * mm});
            skLineSegment(sketch, "E361", {"start": v(-2.53, -0.55) * mm, "end": v(-2.48, -0.32) * mm});
            skLineSegment(sketch, "E362", {"start": v(-2.48, -0.32) * mm, "end": v(-2.41, -0.07) * mm});
            skLineSegment(sketch, "E363", {"start": v(-2.41, -0.07) * mm, "end": v(-2.33, 0.17) * mm});
            skLineSegment(sketch, "E364", {"start": v(-2.33, 0.17) * mm, "end": v(-2.25, 0.4) * mm});
            skLineSegment(sketch, "E365", {"start": v(-2.25, 0.4) * mm, "end": v(-2.16, 0.63) * mm});
            skLineSegment(sketch, "E366", {"start": v(-2.16, 0.63) * mm, "end": v(-2.07, 0.84) * mm});
            skLineSegment(sketch, "E367", {"start": v(-2.07, 0.84) * mm, "end": v(-1.98, 1) * mm});
            skLineSegment(sketch, "E368", {"start": v(-1.98, 1) * mm, "end": v(-1.89, 1.14) * mm});
            skLineSegment(sketch, "E369", {"start": v(-1.89, 1.14) * mm, "end": v(-1.82, 1.23) * mm});
            skLineSegment(sketch, "E370", {"start": v(-1.82, 1.23) * mm, "end": v(-1.76, 1.3) * mm});
            skLineSegment(sketch, "E371", {"start": v(-1.76, 1.3) * mm, "end": v(-1.7, 1.34) * mm});
            skLineSegment(sketch, "E372", {"start": v(-1.7, 1.34) * mm, "end": v(-1.64, 1.37) * mm});
            skLineSegment(sketch, "E373", {"start": v(-1.64, 1.37) * mm, "end": v(-1.59, 1.4) * mm});
            skLineSegment(sketch, "E374", {"start": v(-1.59, 1.4) * mm, "end": v(-1.54, 1.4) * mm});
            skLineSegment(sketch, "E375", {"start": v(-1.54, 1.4) * mm, "end": v(-1.5, 1.38) * mm});
            skLineSegment(sketch, "E376", {"start": v(-1.5, 1.38) * mm, "end": v(-1.46, 1.36) * mm});
            skLineSegment(sketch, "E377", {"start": v(-1.46, 1.36) * mm, "end": v(-1.43, 1.32) * mm});
            skLineSegment(sketch, "E378", {"start": v(-1.43, 1.32) * mm, "end": v(-1.41, 1.26) * mm});
            skLineSegment(sketch, "E379", {"start": v(-1.41, 1.26) * mm, "end": v(-1.4, 1.2) * mm});
            skLineSegment(sketch, "E380", {"start": v(-1.4, 1.2) * mm, "end": v(-1.39, 1.12) * mm});
            skLineSegment(sketch, "E381", {"start": v(-1.39, 1.12) * mm, "end": v(-1.39, 1.03) * mm});
            skLineSegment(sketch, "E382", {"start": v(-1.39, 1.03) * mm, "end": v(-1.4, 0.93) * mm});
            skLineSegment(sketch, "E383", {"start": v(-1.4, 0.93) * mm, "end": v(-1.42, 0.82) * mm});
            skLineSegment(sketch, "E384", {"start": v(-1.42, 0.82) * mm, "end": v(-1.45, 0.7) * mm});
            skLineSegment(sketch, "E385", {"start": v(-1.45, 0.7) * mm, "end": v(-1.53, 0.46) * mm});
            skLineSegment(sketch, "E386", {"start": v(-1.53, 0.46) * mm, "end": v(-1.64, 0.23) * mm});
            skLineSegment(sketch, "E387", {"start": v(-1.64, 0.23) * mm, "end": v(-1.8, -0.02) * mm});
            skLineSegment(sketch, "E388", {"start": v(-1.8, -0.02) * mm, "end": v(-2, -0.3) * mm});
            skLineSegment(sketch, "E389", {"start": v(-2, -0.3) * mm, "end": v(-2.08, -0.4) * mm});
            skLineSegment(sketch, "E390", {"start": v(-2.08, -0.4) * mm, "end": v(-2.14, -0.5) * mm});
            skLineSegment(sketch, "E391", {"start": v(-2.14, -0.5) * mm, "end": v(-2.2, -0.56) * mm});
            skLineSegment(sketch, "E392", {"start": v(-2.2, -0.56) * mm, "end": v(-2.23, -0.62) * mm});
            skLineSegment(sketch, "E393", {"start": v(-2.23, -0.62) * mm, "end": v(-2.25, -0.66) * mm});
            skLineSegment(sketch, "E394", {"start": v(-2.25, -0.66) * mm, "end": v(-2.27, -0.7) * mm});
            skLineSegment(sketch, "E395", {"start": v(-2.27, -0.7) * mm, "end": v(-2.27, -0.74) * mm});
            skLineSegment(sketch, "E396", {"start": v(-2.27, -0.74) * mm, "end": v(-2.27, -0.78) * mm});
            skLineSegment(sketch, "E397", {"start": v(-2.27, -0.78) * mm, "end": v(-2.27, -0.83) * mm});
            skLineSegment(sketch, "E398", {"start": v(-2.27, -0.83) * mm, "end": v(-2.27, -0.88) * mm});
            skLineSegment(sketch, "E399", {"start": v(-2.27, -0.88) * mm, "end": v(-2.26, -0.92) * mm});
            skLineSegment(sketch, "E400", {"start": v(-2.26, -0.92) * mm, "end": v(-2.25, -0.94) * mm});
            skLineSegment(sketch, "E401", {"start": v(-2.25, -0.94) * mm, "end": v(-2.2, -0.98) * mm});
            skLineSegment(sketch, "E402", {"start": v(-2.2, -0.98) * mm, "end": v(-2.13, -0.97) * mm});
            skLineSegment(sketch, "E403", {"start": v(-2.13, -0.97) * mm, "end": v(-2.03, -0.94) * mm});
            skLineSegment(sketch, "E404", {"start": v(-2.03, -0.94) * mm, "end": v(-1.92, -0.87) * mm});
            skLineSegment(sketch, "E405", {"start": v(-1.92, -0.87) * mm, "end": v(-1.87, -0.82) * mm});
            skLineSegment(sketch, "E406", {"start": v(-1.87, -0.82) * mm, "end": v(-1.82, -0.78) * mm});
            skLineSegment(sketch, "E407", {"start": v(-1.82, -0.78) * mm, "end": v(-1.79, -0.74) * mm});
            skLineSegment(sketch, "E408", {"start": v(-1.79, -0.74) * mm, "end": v(-1.76, -0.7) * mm});
            skLineSegment(sketch, "E409", {"start": v(-1.76, -0.7) * mm, "end": v(-1.74, -0.65) * mm});
            skLineSegment(sketch, "E410", {"start": v(-1.74, -0.65) * mm, "end": v(-1.72, -0.6) * mm});
            skLineSegment(sketch, "E411", {"start": v(-1.72, -0.6) * mm, "end": v(-1.7, -0.53) * mm});
            skLineSegment(sketch, "E412", {"start": v(-1.7, -0.53) * mm, "end": v(-1.7, -0.44) * mm});
            skLineSegment(sketch, "E413", {"start": v(-1.7, -0.44) * mm, "end": v(-1.68, -0.37) * mm});
            skLineSegment(sketch, "E414", {"start": v(-1.68, -0.37) * mm, "end": v(-1.65, -0.28) * mm});
            skLineSegment(sketch, "E415", {"start": v(-1.65, -0.28) * mm, "end": v(-1.61, -0.18) * mm});
            skLineSegment(sketch, "E416", {"start": v(-1.61, -0.18) * mm, "end": v(-1.56, -0.08) * mm});
            skLineSegment(sketch, "E417", {"start": v(-1.56, -0.08) * mm, "end": v(-1.5, 0.02) * mm});
            skLineSegment(sketch, "E418", {"start": v(-1.5, 0.02) * mm, "end": v(-1.45, 0.11) * mm});
            skLineSegment(sketch, "E419", {"start": v(-1.45, 0.11) * mm, "end": v(-1.4, 0.19) * mm});
            skLineSegment(sketch, "E420", {"start": v(-1.4, 0.19) * mm, "end": v(-1.34, 0.25) * mm});
            skLineSegment(sketch, "E421", {"start": v(-1.34, 0.25) * mm, "end": v(-1.23, 0.32) * mm});
            skLineSegment(sketch, "E422", {"start": v(-1.23, 0.32) * mm, "end": v(-1.12, 0.36) * mm});
            skLineSegment(sketch, "E423", {"start": v(-1.12, 0.36) * mm, "end": v(-1.01, 0.37) * mm});
            skLineSegment(sketch, "E424", {"start": v(-1.01, 0.37) * mm, "end": v(-0.93, 0.35) * mm});
            skLineSegment(sketch, "E425", {"start": v(-0.93, 0.35) * mm, "end": v(-0.9, 0.32) * mm});
            skLineSegment(sketch, "E426", {"start": v(-0.9, 0.32) * mm, "end": v(-0.88, 0.28) * mm});
            skLineSegment(sketch, "E427", {"start": v(-0.88, 0.28) * mm, "end": v(-0.87, 0.22) * mm});
            skLineSegment(sketch, "E428", {"start": v(-0.87, 0.22) * mm, "end": v(-0.87, 0.14) * mm});
            skLineSegment(sketch, "E429", {"start": v(-0.87, 0.14) * mm, "end": v(-0.88, 0.03) * mm});
            skLineSegment(sketch, "E430", {"start": v(-0.88, 0.03) * mm, "end": v(-0.9, -0.08) * mm});
            skLineSegment(sketch, "E431", {"start": v(-0.9, -0.08) * mm, "end": v(-0.95, -0.19) * mm});
            skLineSegment(sketch, "E432", {"start": v(-0.95, -0.19) * mm, "end": v(-1, -0.3) * mm});
            skLineSegment(sketch, "E433", {"start": v(-1, -0.3) * mm, "end": v(-1.09, -0.4) * mm});
            skLineSegment(sketch, "E434", {"start": v(-1.09, -0.4) * mm, "end": v(-1.18, -0.49) * mm});
            skLineSegment(sketch, "E435", {"start": v(-1.18, -0.49) * mm, "end": v(-1.28, -0.57) * mm});
            skLineSegment(sketch, "E436", {"start": v(-1.28, -0.57) * mm, "end": v(-1.4, -0.65) * mm});
            skLineSegment(sketch, "E437", {"start": v(-1.4, -0.65) * mm, "end": v(-1.44, -0.67) * mm});
            skLineSegment(sketch, "E438", {"start": v(-1.44, -0.67) * mm, "end": v(-1.46, -0.7) * mm});
            skLineSegment(sketch, "E439", {"start": v(-1.46, -0.7) * mm, "end": v(-1.48, -0.7) * mm});
            skLineSegment(sketch, "E440", {"start": v(-1.48, -0.7) * mm, "end": v(-1.5, -0.73) * mm});
            skLineSegment(sketch, "E441", {"start": v(-1.5, -0.73) * mm, "end": v(-1.5, -0.75) * mm});
            skLineSegment(sketch, "E442", {"start": v(-1.5, -0.75) * mm, "end": v(-1.5, -0.77) * mm});
            skLineSegment(sketch, "E443", {"start": v(-1.5, -0.77) * mm, "end": v(-1.5, -0.8) * mm});
            skLineSegment(sketch, "E444", {"start": v(-1.5, -0.8) * mm, "end": v(-1.5, -0.84) * mm});
            skLineSegment(sketch, "E445", {"start": v(-1.5, -0.84) * mm, "end": v(-1.48, -0.93) * mm});
            skLineSegment(sketch, "E446", {"start": v(-1.48, -0.93) * mm, "end": v(-1.45, -1) * mm});
            skLineSegment(sketch, "E447", {"start": v(-1.45, -1) * mm, "end": v(-1.4, -1.05) * mm});
            skLineSegment(sketch, "E448", {"start": v(-1.4, -1.05) * mm, "end": v(-1.36, -1.08) * mm});
            skLineSegment(sketch, "E449", {"start": v(-1.36, -1.08) * mm, "end": v(-1.3, -1.1) * mm});
            skLineSegment(sketch, "E450", {"start": v(-1.3, -1.1) * mm, "end": v(-1.25, -1.09) * mm});
            skLineSegment(sketch, "E451", {"start": v(-1.25, -1.09) * mm, "end": v(-1.18, -1.06) * mm});
            skLineSegment(sketch, "E452", {"start": v(-1.18, -1.06) * mm, "end": v(-1.1, -1.02) * mm});
            skLineSegment(sketch, "E453", {"start": v(-1.1, -1.02) * mm, "end": v(-1.05, -0.98) * mm});
            skLineSegment(sketch, "E454", {"start": v(-1.05, -0.98) * mm, "end": v(-1, -0.92) * mm});
            skLineSegment(sketch, "E455", {"start": v(-1, -0.92) * mm, "end": v(-0.94, -0.86) * mm});
            skLineSegment(sketch, "E456", {"start": v(-0.94, -0.86) * mm, "end": v(-0.9, -0.8) * mm});
            skLineSegment(sketch, "E457", {"start": v(-0.9, -0.8) * mm, "end": v(-0.87, -0.74) * mm});
            skLineSegment(sketch, "E458", {"start": v(-0.87, -0.74) * mm, "end": v(-0.85, -0.7) * mm});
            skLineSegment(sketch, "E459", {"start": v(-0.85, -0.7) * mm, "end": v(-0.82, -0.67) * mm});
            skLineSegment(sketch, "E460", {"start": v(-0.82, -0.67) * mm, "end": v(-0.8, -0.66) * mm});
            skLineSegment(sketch, "E461", {"start": v(-0.8, -0.66) * mm, "end": v(-0.79, -0.66) * mm});
            skLineSegment(sketch, "E462", {"start": v(-0.79, -0.66) * mm, "end": v(-0.77, -0.68) * mm});
            skLineSegment(sketch, "E463", {"start": v(-0.77, -0.68) * mm, "end": v(-0.76, -0.7) * mm});
            skLineSegment(sketch, "E464", {"start": v(-0.76, -0.7) * mm, "end": v(-0.76, -0.74) * mm});
            skLineSegment(sketch, "E465", {"start": v(-0.76, -0.74) * mm, "end": v(-0.76, -0.79) * mm});
            skLineSegment(sketch, "E466", {"start": v(-0.76, -0.79) * mm, "end": v(-0.78, -0.84) * mm});
            skLineSegment(sketch, "E467", {"start": v(-0.78, -0.84) * mm, "end": v(-0.81, -0.9) * mm});
            skLineSegment(sketch, "E468", {"start": v(-0.81, -0.9) * mm, "end": v(-0.85, -0.96) * mm});
            skLineSegment(sketch, "E469", {"start": v(-0.85, -0.96) * mm, "end": v(-0.9, -1.02) * mm});
            skLineSegment(sketch, "E470", {"start": v(-0.9, -1.02) * mm, "end": v(-0.96, -1.08) * mm});
            skLineSegment(sketch, "E471", {"start": v(-0.96, -1.08) * mm, "end": v(-1.02, -1.13) * mm});
            skLineSegment(sketch, "E472", {"start": v(-1.02, -1.13) * mm, "end": v(-1.08, -1.17) * mm});
            skLineSegment(sketch, "E473", {"start": v(-1.08, -1.17) * mm, "end": v(-1.2, -1.22) * mm});
            skLineSegment(sketch, "E474", {"start": v(-1.2, -1.22) * mm, "end": v(-1.35, -1.24) * mm});
            skLineSegment(sketch, "E475", {"start": v(-1.35, -1.24) * mm, "end": v(-1.48, -1.23) * mm});
            skLineSegment(sketch, "E476", {"start": v(-1.48, -1.23) * mm, "end": v(-1.58, -1.19) * mm});
            skLineSegment(sketch, "E477", {"start": v(-1.58, -1.19) * mm, "end": v(-1.6, -1.16) * mm});
            skLineSegment(sketch, "E478", {"start": v(-1.6, -1.16) * mm, "end": v(-1.64, -1.11) * mm});
            skLineSegment(sketch, "E479", {"start": v(-1.64, -1.11) * mm, "end": v(-1.66, -1.07) * mm});
            skLineSegment(sketch, "E480", {"start": v(-1.66, -1.07) * mm, "end": v(-1.68, -1.02) * mm});
            skLineSegment(sketch, "E481", {"start": v(-1.68, -1.02) * mm, "end": v(-1.72, -0.9) * mm});
            skLineSegment(sketch, "E482", {"start": v(-1.72, -0.9) * mm, "end": v(-1.85, -1.02) * mm});
            skLineSegment(sketch, "E483", {"start": v(-1.85, -1.02) * mm, "end": v(-1.97, -1.12) * mm});
            skLineSegment(sketch, "E484", {"start": v(-1.97, -1.12) * mm, "end": v(-2.08, -1.2) * mm});
            skLineSegment(sketch, "E485", {"start": v(-2.08, -1.2) * mm, "end": v(-2.19, -1.23) * mm});
            skLineSegment(sketch, "E486", {"start": v(-2.19, -1.23) * mm, "end": v(-2.29, -1.25) * mm});
            skLineSegment(sketch, "E487", {"start": v(-2.29, -1.25) * mm, "end": v(-2.37, -1.24) * mm});
            skLineSegment(sketch, "E488", {"start": v(-2.37, -1.24) * mm, "end": v(-2.44, -1.2) * mm});
            skLineSegment(sketch, "E489", {"start": v(-2.44, -1.2) * mm, "end": v(-2.49, -1.14) * mm});
            skLineSegment(sketch, "E490", {"start": v(-2.49, -1.14) * mm, "end": v(-2.53, -1.05) * mm});
            skLineSegment(sketch, "E491", {"start": v(-2.53, -1.05) * mm, "end": v(-2.57, -0.94) * mm});
            skLineSegment(sketch, "E492", {"start": v(-2.57, -0.94) * mm, "end": v(-2.65, -1.02) * mm});
            skLineSegment(sketch, "E493", {"start": v(-2.65, -1.02) * mm, "end": v(-2.8, -1.14) * mm});
            skLineSegment(sketch, "E494", {"start": v(-2.8, -1.14) * mm, "end": v(-2.96, -1.22) * mm});
            skLineSegment(sketch, "E495", {"start": v(-2.96, -1.22) * mm, "end": v(-3.11, -1.25) * mm});
            skLineSegment(sketch, "E496", {"start": v(-3.11, -1.25) * mm, "end": v(-3.24, -1.22) * mm});
            skLineSegment(sketch, "E497", {"start": v(-3.24, -1.22) * mm, "end": v(-3.26, -1.2) * mm});
            skLineSegment(sketch, "E498", {"start": v(-3.26, -1.2) * mm, "end": v(-3.29, -1.17) * mm});
            skLineSegment(sketch, "E499", {"start": v(-3.29, -1.17) * mm, "end": v(-3.3, -1.14) * mm});
            skLineSegment(sketch, "E500", {"start": v(-3.3, -1.14) * mm, "end": v(-3.33, -1.1) * mm});
            skLineSegment(sketch, "E501", {"start": v(-3.33, -1.1) * mm, "end": v(-3.37, -0.98) * mm});
            skLineSegment(sketch, "E502", {"start": v(-3.37, -0.98) * mm, "end": v(-3.47, -1.06) * mm});
            skLineSegment(sketch, "E503", {"start": v(-3.47, -1.06) * mm, "end": v(-3.66, -1.17) * mm});
            skLineSegment(sketch, "E504", {"start": v(-3.66, -1.17) * mm, "end": v(-3.88, -1.24) * mm});
            skLineSegment(sketch, "E505", {"start": v(-3.88, -1.24) * mm, "end": v(-4.1, -1.27) * mm});
            skLineSegment(sketch, "E506", {"start": v(-4.1, -1.27) * mm, "end": v(-4.3, -1.24) * mm});
            skLineSegment(sketch, "E507", {"start": v(-1.38, -0.49) * mm, "end": v(-1.3, -0.42) * mm});
            skLineSegment(sketch, "E508", {"start": v(-1.3, -0.42) * mm, "end": v(-1.23, -0.34) * mm});
            skLineSegment(sketch, "E509", {"start": v(-1.23, -0.34) * mm, "end": v(-1.16, -0.25) * mm});
            skLineSegment(sketch, "E510", {"start": v(-1.16, -0.25) * mm, "end": v(-1.1, -0.15) * mm});
            skLineSegment(sketch, "E511", {"start": v(-1.1, -0.15) * mm, "end": v(-1.06, -0.05) * mm});
            skLineSegment(sketch, "E512", {"start": v(-1.06, -0.05) * mm, "end": v(-1.03, 0.04) * mm});
            skLineSegment(sketch, "E513", {"start": v(-1.03, 0.04) * mm, "end": v(-1.02, 0.11) * mm});
            skLineSegment(sketch, "E514", {"start": v(-1.02, 0.11) * mm, "end": v(-1.04, 0.16) * mm});
            skLineSegment(sketch, "E515", {"start": v(-1.04, 0.16) * mm, "end": v(-1.07, 0.17) * mm});
            skLineSegment(sketch, "E516", {"start": v(-1.07, 0.17) * mm, "end": v(-1.1, 0.14) * mm});
            skLineSegment(sketch, "E517", {"start": v(-1.1, 0.14) * mm, "end": v(-1.16, 0.08) * mm});
            skLineSegment(sketch, "E518", {"start": v(-1.16, 0.08) * mm, "end": v(-1.23, 0) * mm});
            skLineSegment(sketch, "E519", {"start": v(-1.23, 0) * mm, "end": v(-1.29, -0.1) * mm});
            skLineSegment(sketch, "E520", {"start": v(-1.29, -0.1) * mm, "end": v(-1.35, -0.19) * mm});
            skLineSegment(sketch, "E521", {"start": v(-1.35, -0.19) * mm, "end": v(-1.4, -0.28) * mm});
            skLineSegment(sketch, "E522", {"start": v(-1.4, -0.28) * mm, "end": v(-1.43, -0.37) * mm});
            skLineSegment(sketch, "E523", {"start": v(-1.43, -0.37) * mm, "end": v(-1.44, -0.42) * mm});
            skLineSegment(sketch, "E524", {"start": v(-1.44, -0.42) * mm, "end": v(-1.45, -0.47) * mm});
            skLineSegment(sketch, "E525", {"start": v(-1.45, -0.47) * mm, "end": v(-1.46, -0.5) * mm});
            skLineSegment(sketch, "E526", {"start": v(-1.46, -0.5) * mm, "end": v(-1.46, -0.52) * mm});
            skLineSegment(sketch, "E527", {"start": v(-1.46, -0.52) * mm, "end": v(-1.45, -0.52) * mm});
            skLineSegment(sketch, "E528", {"start": v(-1.45, -0.52) * mm, "end": v(-1.44, -0.52) * mm});
            skLineSegment(sketch, "E529", {"start": v(-1.44, -0.52) * mm, "end": v(-1.41, -0.5) * mm});
            skLineSegment(sketch, "E530", {"start": v(-1.41, -0.5) * mm, "end": v(-1.38, -0.49) * mm});
            skLineSegment(sketch, "E531", {"start": v(-2.66, 0.18) * mm, "end": v(-2.57, 0.34) * mm});
            skLineSegment(sketch, "E532", {"start": v(-2.57, 0.34) * mm, "end": v(-2.5, 0.5) * mm});
            skLineSegment(sketch, "E533", {"start": v(-2.5, 0.5) * mm, "end": v(-2.44, 0.66) * mm});
            skLineSegment(sketch, "E534", {"start": v(-2.44, 0.66) * mm, "end": v(-2.4, 0.8) * mm});
            skLineSegment(sketch, "E535", {"start": v(-2.4, 0.8) * mm, "end": v(-2.36, 0.94) * mm});
            skLineSegment(sketch, "E536", {"start": v(-2.36, 0.94) * mm, "end": v(-2.35, 1.04) * mm});
            skLineSegment(sketch, "E537", {"start": v(-2.35, 1.04) * mm, "end": v(-2.36, 1.11) * mm});
            skLineSegment(sketch, "E538", {"start": v(-2.36, 1.11) * mm, "end": v(-2.39, 1.14) * mm});
            skLineSegment(sketch, "E539", {"start": v(-2.39, 1.14) * mm, "end": v(-2.41, 1.12) * mm});
            skLineSegment(sketch, "E540", {"start": v(-2.41, 1.12) * mm, "end": v(-2.45, 1.1) * mm});
            skLineSegment(sketch, "E541", {"start": v(-2.45, 1.1) * mm, "end": v(-2.49, 1.04) * mm});
            skLineSegment(sketch, "E542", {"start": v(-2.49, 1.04) * mm, "end": v(-2.53, 0.98) * mm});
            skLineSegment(sketch, "E543", {"start": v(-2.53, 0.98) * mm, "end": v(-2.58, 0.9) * mm});
            skLineSegment(sketch, "E544", {"start": v(-2.58, 0.9) * mm, "end": v(-2.63, 0.81) * mm});
            skLineSegment(sketch, "E545", {"start": v(-2.63, 0.81) * mm, "end": v(-2.67, 0.72) * mm});
            skLineSegment(sketch, "E546", {"start": v(-2.67, 0.72) * mm, "end": v(-2.72, 0.63) * mm});
            skLineSegment(sketch, "E547", {"start": v(-2.72, 0.63) * mm, "end": v(-2.76, 0.52) * mm});
            skLineSegment(sketch, "E548", {"start": v(-2.76, 0.52) * mm, "end": v(-2.81, 0.39) * mm});
            skLineSegment(sketch, "E549", {"start": v(-2.81, 0.39) * mm, "end": v(-2.86, 0.24) * mm});
            skLineSegment(sketch, "E550", {"start": v(-2.86, 0.24) * mm, "end": v(-2.91, 0.1) * mm});
            skLineSegment(sketch, "E551", {"start": v(-2.91, 0.1) * mm, "end": v(-2.95, -0.04) * mm});
            skLineSegment(sketch, "E552", {"start": v(-2.95, -0.04) * mm, "end": v(-3, -0.16) * mm});
            skLineSegment(sketch, "E553", {"start": v(-3, -0.16) * mm, "end": v(-3.01, -0.25) * mm});
            skLineSegment(sketch, "E554", {"start": v(-3.01, -0.25) * mm, "end": v(-3.02, -0.3) * mm});
            skLineSegment(sketch, "E555", {"start": v(-3.02, -0.3) * mm, "end": v(-3.01, -0.32) * mm});
            skLineSegment(sketch, "E556", {"start": v(-3.01, -0.32) * mm, "end": v(-2.99, -0.3) * mm});
            skLineSegment(sketch, "E557", {"start": v(-2.99, -0.3) * mm, "end": v(-2.94, -0.25) * mm});
            skLineSegment(sketch, "E558", {"start": v(-2.94, -0.25) * mm, "end": v(-2.9, -0.19) * mm});
            skLineSegment(sketch, "E559", {"start": v(-2.9, -0.19) * mm, "end": v(-2.84, -0.1) * mm});
            skLineSegment(sketch, "E560", {"start": v(-2.84, -0.1) * mm, "end": v(-2.77, -0.02) * mm});
            skLineSegment(sketch, "E561", {"start": v(-2.77, -0.02) * mm, "end": v(-2.71, 0.08) * mm});
            skLineSegment(sketch, "E562", {"start": v(-2.71, 0.08) * mm, "end": v(-2.66, 0.18) * mm});
            skLineSegment(sketch, "E563", {"start": v(-1.74, 0.38) * mm, "end": v(-1.68, 0.51) * mm});
            skLineSegment(sketch, "E564", {"start": v(-1.68, 0.51) * mm, "end": v(-1.63, 0.65) * mm});
            skLineSegment(sketch, "E565", {"start": v(-1.63, 0.65) * mm, "end": v(-1.6, 0.78) * mm});
            skLineSegment(sketch, "E566", {"start": v(-1.6, 0.78) * mm, "end": v(-1.56, 0.9) * mm});
            skLineSegment(sketch, "E567", {"start": v(-1.56, 0.9) * mm, "end": v(-1.54, 1) * mm});
            skLineSegment(sketch, "E568", {"start": v(-1.54, 1) * mm, "end": v(-1.53, 1.07) * mm});
            skLineSegment(sketch, "E569", {"start": v(-1.53, 1.07) * mm, "end": v(-1.54, 1.12) * mm});
            skLineSegment(sketch, "E570", {"start": v(-1.54, 1.12) * mm, "end": v(-1.56, 1.14) * mm});
            skLineSegment(sketch, "E571", {"start": v(-1.56, 1.14) * mm, "end": v(-1.61, 1.11) * mm});
            skLineSegment(sketch, "E572", {"start": v(-1.61, 1.11) * mm, "end": v(-1.68, 1.04) * mm});
            skLineSegment(sketch, "E573", {"start": v(-1.68, 1.04) * mm, "end": v(-1.75, 0.93) * mm});
            skLineSegment(sketch, "E574", {"start": v(-1.75, 0.93) * mm, "end": v(-1.83, 0.8) * mm});
            skLineSegment(sketch, "E575", {"start": v(-1.83, 0.8) * mm, "end": v(-1.88, 0.69) * mm});
            skLineSegment(sketch, "E576", {"start": v(-1.88, 0.69) * mm, "end": v(-1.93, 0.56) * mm});
            skLineSegment(sketch, "E577", {"start": v(-1.93, 0.56) * mm, "end": v(-1.99, 0.4) * mm});
            skLineSegment(sketch, "E578", {"start": v(-1.99, 0.4) * mm, "end": v(-2.04, 0.25) * mm});
            skLineSegment(sketch, "E579", {"start": v(-2.04, 0.25) * mm, "end": v(-2.1, 0.1) * mm});
            skLineSegment(sketch, "E580", {"start": v(-2.1, 0.1) * mm, "end": v(-2.14, -0.04) * mm});
            skLineSegment(sketch, "E581", {"start": v(-2.14, -0.04) * mm, "end": v(-2.17, -0.16) * mm});
            skLineSegment(sketch, "E582", {"start": v(-2.17, -0.16) * mm, "end": v(-2.2, -0.24) * mm});
            skLineSegment(sketch, "E583", {"start": v(-2.2, -0.24) * mm, "end": v(-2.2, -0.28) * mm});
            skLineSegment(sketch, "E584", {"start": v(-2.2, -0.28) * mm, "end": v(-2.2, -0.3) * mm});
            skLineSegment(sketch, "E585", {"start": v(-2.2, -0.3) * mm, "end": v(-2.2, -0.3) * mm});
            skLineSegment(sketch, "E586", {"start": v(-2.2, -0.3) * mm, "end": v(-2.18, -0.3) * mm});
            skLineSegment(sketch, "E587", {"start": v(-2.18, -0.3) * mm, "end": v(-2.16, -0.28) * mm});
            skLineSegment(sketch, "E588", {"start": v(-2.16, -0.28) * mm, "end": v(-2.13, -0.24) * mm});
            skLineSegment(sketch, "E589", {"start": v(-2.13, -0.24) * mm, "end": v(-2.09, -0.19) * mm});
            skLineSegment(sketch, "E590", {"start": v(-2.09, -0.19) * mm, "end": v(-2.03, -0.11) * mm});
            skLineSegment(sketch, "E591", {"start": v(-2.03, -0.11) * mm, "end": v(-1.95, 0) * mm});
            skLineSegment(sketch, "E592", {"start": v(-1.95, 0) * mm, "end": v(-1.87, 0.13) * mm});
            skLineSegment(sketch, "E593", {"start": v(-1.87, 0.13) * mm, "end": v(-1.8, 0.27) * mm});
            skLineSegment(sketch, "E594", {"start": v(-1.8, 0.27) * mm, "end": v(-1.74, 0.38) * mm});
            skLineSegment(sketch, "E595", {"start": v(-0.45, -1.12) * mm, "end": v(-0.5, -1.03) * mm});
            skLineSegment(sketch, "E596", {"start": v(-0.5, -1.03) * mm, "end": v(-0.53, -0.94) * mm});
            skLineSegment(sketch, "E597", {"start": v(-0.53, -0.94) * mm, "end": v(-0.55, -0.85) * mm});
            skLineSegment(sketch, "E598", {"start": v(-0.55, -0.85) * mm, "end": v(-0.54, -0.75) * mm});
            skLineSegment(sketch, "E599", {"start": v(-0.54, -0.75) * mm, "end": v(-0.52, -0.66) * mm});
            skLineSegment(sketch, "E600", {"start": v(-0.52, -0.66) * mm, "end": v(-0.48, -0.57) * mm});
            skLineSegment(sketch, "E601", {"start": v(-0.48, -0.57) * mm, "end": v(-0.42, -0.49) * mm});
            skLineSegment(sketch, "E602", {"start": v(-0.42, -0.49) * mm, "end": v(-0.35, -0.41) * mm});
            skLineSegment(sketch, "E603", {"start": v(-0.35, -0.41) * mm, "end": v(-0.31, -0.38) * mm});
            skLineSegment(sketch, "E604", {"start": v(-0.31, -0.38) * mm, "end": v(-0.28, -0.36) * mm});
            skLineSegment(sketch, "E605", {"start": v(-0.28, -0.36) * mm, "end": v(-0.26, -0.33) * mm});
            skLineSegment(sketch, "E606", {"start": v(-0.26, -0.33) * mm, "end": v(-0.25, -0.3) * mm});
            skLineSegment(sketch, "E607", {"start": v(-0.25, -0.3) * mm, "end": v(-0.24, -0.28) * mm});
            skLineSegment(sketch, "E608", {"start": v(-0.24, -0.28) * mm, "end": v(-0.24, -0.24) * mm});
            skLineSegment(sketch, "E609", {"start": v(-0.24, -0.24) * mm, "end": v(-0.24, -0.2) * mm});
            skLineSegment(sketch, "E610", {"start": v(-0.24, -0.2) * mm, "end": v(-0.25, -0.13) * mm});
            skLineSegment(sketch, "E611", {"start": v(-0.25, -0.13) * mm, "end": v(-0.25, -0.03) * mm});
            skLineSegment(sketch, "E612", {"start": v(-0.25, -0.03) * mm, "end": v(-0.25, 0.04) * mm});
            skLineSegment(sketch, "E613", {"start": v(-0.25, 0.04) * mm, "end": v(-0.23, 0.1) * mm});
            skLineSegment(sketch, "E614", {"start": v(-0.23, 0.1) * mm, "end": v(-0.2, 0.17) * mm});
            skLineSegment(sketch, "E615", {"start": v(-0.2, 0.17) * mm, "end": v(-0.09, 0.3) * mm});
            skLineSegment(sketch, "E616", {"start": v(-0.09, 0.3) * mm, "end": v(0.04, 0.36) * mm});
            skLineSegment(sketch, "E617", {"start": v(0.04, 0.36) * mm, "end": v(0.17, 0.37) * mm});
            skLineSegment(sketch, "E618", {"start": v(0.17, 0.37) * mm, "end": v(0.3, 0.32) * mm});
            skLineSegment(sketch, "E619", {"start": v(0.3, 0.32) * mm, "end": v(0.34, 0.29) * mm});
            skLineSegment(sketch, "E620", {"start": v(0.34, 0.29) * mm, "end": v(0.37, 0.25) * mm});
            skLineSegment(sketch, "E621", {"start": v(0.37, 0.25) * mm, "end": v(0.38, 0.21) * mm});
            skLineSegment(sketch, "E622", {"start": v(0.38, 0.21) * mm, "end": v(0.39, 0.16) * mm});
            skLineSegment(sketch, "E623", {"start": v(0.39, 0.16) * mm, "end": v(0.37, 0.06) * mm});
            skLineSegment(sketch, "E624", {"start": v(0.37, 0.06) * mm, "end": v(0.33, -0.03) * mm});
            skLineSegment(sketch, "E625", {"start": v(0.33, -0.03) * mm, "end": v(0.26, -0.12) * mm});
            skLineSegment(sketch, "E626", {"start": v(0.26, -0.12) * mm, "end": v(0.15, -0.22) * mm});
            skLineSegment(sketch, "E627", {"start": v(0.15, -0.22) * mm, "end": v(0.1, -0.27) * mm});
            skLineSegment(sketch, "E628", {"start": v(0.1, -0.27) * mm, "end": v(0.06, -0.3) * mm});
            skLineSegment(sketch, "E629", {"start": v(0.06, -0.3) * mm, "end": v(0.04, -0.34) * mm});
            skLineSegment(sketch, "E630", {"start": v(0.04, -0.34) * mm, "end": v(0.03, -0.38) * mm});
            skLineSegment(sketch, "E631", {"start": v(0.03, -0.38) * mm, "end": v(0.04, -0.42) * mm});
            skLineSegment(sketch, "E632", {"start": v(0.04, -0.42) * mm, "end": v(0.07, -0.47) * mm});
            skLineSegment(sketch, "E633", {"start": v(0.07, -0.47) * mm, "end": v(0.1, -0.54) * mm});
            skLineSegment(sketch, "E634", {"start": v(0.1, -0.54) * mm, "end": v(0.17, -0.62) * mm});
            skLineSegment(sketch, "E635", {"start": v(0.17, -0.62) * mm, "end": v(0.27, -0.77) * mm});
            skLineSegment(sketch, "E636", {"start": v(0.27, -0.77) * mm, "end": v(0.36, -0.64) * mm});
            skLineSegment(sketch, "E637", {"start": v(0.36, -0.64) * mm, "end": v(0.4, -0.58) * mm});
            skLineSegment(sketch, "E638", {"start": v(0.4, -0.58) * mm, "end": v(0.43, -0.52) * mm});
            skLineSegment(sketch, "E639", {"start": v(0.43, -0.52) * mm, "end": v(0.46, -0.45) * mm});
            skLineSegment(sketch, "E640", {"start": v(0.46, -0.45) * mm, "end": v(0.49, -0.39) * mm});
            skLineSegment(sketch, "E641", {"start": v(0.49, -0.39) * mm, "end": v(0.5, -0.34) * mm});
            skLineSegment(sketch, "E642", {"start": v(0.5, -0.34) * mm, "end": v(0.53, -0.3) * mm});
            skLineSegment(sketch, "E643", {"start": v(0.53, -0.3) * mm, "end": v(0.55, -0.28) * mm});
            skLineSegment(sketch, "E644", {"start": v(0.55, -0.28) * mm, "end": v(0.56, -0.28) * mm});
            skLineSegment(sketch, "E645", {"start": v(0.56, -0.28) * mm, "end": v(0.59, -0.34) * mm});
            skLineSegment(sketch, "E646", {"start": v(0.59, -0.34) * mm, "end": v(0.59, -0.45) * mm});
            skLineSegment(sketch, "E647", {"start": v(0.59, -0.45) * mm, "end": v(0.56, -0.58) * mm});
            skLineSegment(sketch, "E648", {"start": v(0.56, -0.58) * mm, "end": v(0.52, -0.71) * mm});
            skLineSegment(sketch, "E649", {"start": v(0.52, -0.71) * mm, "end": v(0.49, -0.78) * mm});
            skLineSegment(sketch, "E650", {"start": v(0.49, -0.78) * mm, "end": v(0.47, -0.84) * mm});
            skLineSegment(sketch, "E651", {"start": v(0.47, -0.84) * mm, "end": v(0.45, -0.88) * mm});
            skLineSegment(sketch, "E652", {"start": v(0.45, -0.88) * mm, "end": v(0.44, -0.91) * mm});
            skLineSegment(sketch, "E653", {"start": v(0.44, -0.91) * mm, "end": v(0.45, -0.93) * mm});
            skLineSegment(sketch, "E654", {"start": v(0.45, -0.93) * mm, "end": v(0.48, -0.96) * mm});
            skLineSegment(sketch, "E655", {"start": v(0.48, -0.96) * mm, "end": v(0.52, -1) * mm});
            skLineSegment(sketch, "E656", {"start": v(0.52, -1) * mm, "end": v(0.57, -1.02) * mm});
            skLineSegment(sketch, "E657", {"start": v(0.57, -1.02) * mm, "end": v(0.62, -1.05) * mm});
            skLineSegment(sketch, "E658", {"start": v(0.62, -1.05) * mm, "end": v(0.68, -1.07) * mm});
            skLineSegment(sketch, "E659", {"start": v(0.68, -1.07) * mm, "end": v(0.72, -1.09) * mm});
            skLineSegment(sketch, "E660", {"start": v(0.72, -1.09) * mm, "end": v(0.76, -1.1) * mm});
            skLineSegment(sketch, "E661", {"start": v(0.76, -1.1) * mm, "end": v(0.8, -1.1) * mm});
            skLineSegment(sketch, "E662", {"start": v(0.8, -1.1) * mm, "end": v(0.81, -1.1) * mm});
            skLineSegment(sketch, "E663", {"start": v(0.81, -1.1) * mm, "end": v(0.8, -1.12) * mm});
            skLineSegment(sketch, "E664", {"start": v(0.8, -1.12) * mm, "end": v(0.8, -1.15) * mm});
            skLineSegment(sketch, "E665", {"start": v(0.8, -1.15) * mm, "end": v(0.73, -1.2) * mm});
            skLineSegment(sketch, "E666", {"start": v(0.73, -1.2) * mm, "end": v(0.63, -1.2) * mm});
            skLineSegment(sketch, "E667", {"start": v(0.63, -1.2) * mm, "end": v(0.52, -1.19) * mm});
            skLineSegment(sketch, "E668", {"start": v(0.52, -1.19) * mm, "end": v(0.42, -1.14) * mm});
            skLineSegment(sketch, "E669", {"start": v(0.42, -1.14) * mm, "end": v(0.39, -1.11) * mm});
            skLineSegment(sketch, "E670", {"start": v(0.39, -1.11) * mm, "end": v(0.36, -1.1) * mm});
            skLineSegment(sketch, "E671", {"start": v(0.36, -1.1) * mm, "end": v(0.34, -1.1) * mm});
            skLineSegment(sketch, "E672", {"start": v(0.34, -1.1) * mm, "end": v(0.32, -1.09) * mm});
            skLineSegment(sketch, "E673", {"start": v(0.32, -1.09) * mm, "end": v(0.3, -1.1) * mm});
            skLineSegment(sketch, "E674", {"start": v(0.3, -1.1) * mm, "end": v(0.27, -1.1) * mm});
            skLineSegment(sketch, "E675", {"start": v(0.27, -1.1) * mm, "end": v(0.24, -1.13) * mm});
            skLineSegment(sketch, "E676", {"start": v(0.24, -1.13) * mm, "end": v(0.2, -1.16) * mm});
            skLineSegment(sketch, "E677", {"start": v(0.2, -1.16) * mm, "end": v(0.13, -1.2) * mm});
            skLineSegment(sketch, "E678", {"start": v(0.13, -1.2) * mm, "end": v(0.06, -1.23) * mm});
            skLineSegment(sketch, "E679", {"start": v(0.06, -1.23) * mm, "end": v(-0.02, -1.24) * mm});
            skLineSegment(sketch, "E680", {"start": v(-0.02, -1.24) * mm, "end": v(-0.13, -1.25) * mm});
            skLineSegment(sketch, "E681", {"start": v(-0.13, -1.25) * mm, "end": v(-0.2, -1.25) * mm});
            skLineSegment(sketch, "E682", {"start": v(-0.2, -1.25) * mm, "end": v(-0.26, -1.24) * mm});
            skLineSegment(sketch, "E683", {"start": v(-0.26, -1.24) * mm, "end": v(-0.3, -1.24) * mm});
            skLineSegment(sketch, "E684", {"start": v(-0.3, -1.24) * mm, "end": v(-0.33, -1.23) * mm});
            skLineSegment(sketch, "E685", {"start": v(-0.33, -1.23) * mm, "end": v(-0.36, -1.21) * mm});
            skLineSegment(sketch, "E686", {"start": v(-0.36, -1.21) * mm, "end": v(-0.39, -1.19) * mm});
            skLineSegment(sketch, "E687", {"start": v(-0.39, -1.19) * mm, "end": v(-0.42, -1.16) * mm});
            skLineSegment(sketch, "E688", {"start": v(-0.42, -1.16) * mm, "end": v(-0.45, -1.12) * mm});
            skLineSegment(sketch, "E689", {"start": v(0.07, -1) * mm, "end": v(0.16, -0.94) * mm});
            skLineSegment(sketch, "E690", {"start": v(0.16, -0.94) * mm, "end": v(0, -0.72) * mm});
            skLineSegment(sketch, "E691", {"start": v(0, -0.72) * mm, "end": v(-0.06, -0.64) * mm});
            skLineSegment(sketch, "E692", {"start": v(-0.06, -0.64) * mm, "end": v(-0.1, -0.57) * mm});
            skLineSegment(sketch, "E693", {"start": v(-0.1, -0.57) * mm, "end": v(-0.15, -0.52) * mm});
            skLineSegment(sketch, "E694", {"start": v(-0.15, -0.52) * mm, "end": v(-0.17, -0.5) * mm});
            skLineSegment(sketch, "E695", {"start": v(-0.17, -0.5) * mm, "end": v(-0.19, -0.5) * mm});
            skLineSegment(sketch, "E696", {"start": v(-0.19, -0.5) * mm, "end": v(-0.2, -0.53) * mm});
            skLineSegment(sketch, "E697", {"start": v(-0.2, -0.53) * mm, "end": v(-0.24, -0.56) * mm});
            skLineSegment(sketch, "E698", {"start": v(-0.24, -0.56) * mm, "end": v(-0.27, -0.6) * mm});
            skLineSegment(sketch, "E699", {"start": v(-0.27, -0.6) * mm, "end": v(-0.3, -0.66) * mm});
            skLineSegment(sketch, "E700", {"start": v(-0.3, -0.66) * mm, "end": v(-0.32, -0.71) * mm});
            skLineSegment(sketch, "E701", {"start": v(-0.32, -0.71) * mm, "end": v(-0.34, -0.76) * mm});
            skLineSegment(sketch, "E702", {"start": v(-0.34, -0.76) * mm, "end": v(-0.34, -0.8) * mm});
            skLineSegment(sketch, "E703", {"start": v(-0.34, -0.8) * mm, "end": v(-0.34, -0.82) * mm});
            skLineSegment(sketch, "E704", {"start": v(-0.34, -0.82) * mm, "end": v(-0.32, -0.87) * mm});
            skLineSegment(sketch, "E705", {"start": v(-0.32, -0.87) * mm, "end": v(-0.3, -0.91) * mm});
            skLineSegment(sketch, "E706", {"start": v(-0.3, -0.91) * mm, "end": v(-0.28, -0.96) * mm});
            skLineSegment(sketch, "E707", {"start": v(-0.28, -0.96) * mm, "end": v(-0.22, -1.03) * mm});
            skLineSegment(sketch, "E708", {"start": v(-0.22, -1.03) * mm, "end": v(-0.13, -1.06) * mm});
            skLineSegment(sketch, "E709", {"start": v(-0.13, -1.06) * mm, "end": v(-0.03, -1.05) * mm});
            skLineSegment(sketch, "E710", {"start": v(-0.03, -1.05) * mm, "end": v(0.07, -1) * mm});
            skLineSegment(sketch, "E711", {"start": v(0.08, -0.1) * mm, "end": v(0.16, -0.03) * mm});
            skLineSegment(sketch, "E712", {"start": v(0.16, -0.03) * mm, "end": v(0.21, 0.04) * mm});
            skLineSegment(sketch, "E713", {"start": v(0.21, 0.04) * mm, "end": v(0.23, 0.12) * mm});
            skLineSegment(sketch, "E714", {"start": v(0.23, 0.12) * mm, "end": v(0.21, 0.2) * mm});
            skLineSegment(sketch, "E715", {"start": v(0.21, 0.2) * mm, "end": v(0.17, 0.24) * mm});
            skLineSegment(sketch, "E716", {"start": v(0.17, 0.24) * mm, "end": v(0.12, 0.26) * mm});
            skLineSegment(sketch, "E717", {"start": v(0.12, 0.26) * mm, "end": v(0.05, 0.25) * mm});
            skLineSegment(sketch, "E718", {"start": v(0.05, 0.25) * mm, "end": v(-0.02, 0.2) * mm});
            skLineSegment(sketch, "E719", {"start": v(-0.02, 0.2) * mm, "end": v(-0.05, 0.17) * mm});
            skLineSegment(sketch, "E720", {"start": v(-0.05, 0.17) * mm, "end": v(-0.07, 0.13) * mm});
            skLineSegment(sketch, "E721", {"start": v(-0.07, 0.13) * mm, "end": v(-0.08, 0.06) * mm});
            skLineSegment(sketch, "E722", {"start": v(-0.08, 0.06) * mm, "end": v(-0.08, -0.02) * mm});
            skLineSegment(sketch, "E723", {"start": v(-0.08, -0.02) * mm, "end": v(-0.08, -0.08) * mm});
            skLineSegment(sketch, "E724", {"start": v(-0.08, -0.08) * mm, "end": v(-0.07, -0.13) * mm});
            skLineSegment(sketch, "E725", {"start": v(-0.07, -0.13) * mm, "end": v(-0.07, -0.16) * mm});
            skLineSegment(sketch, "E726", {"start": v(-0.07, -0.16) * mm, "end": v(-0.05, -0.18) * mm});
            skLineSegment(sketch, "E727", {"start": v(-0.05, -0.18) * mm, "end": v(-0.03, -0.18) * mm});
            skLineSegment(sketch, "E728", {"start": v(-0.03, -0.18) * mm, "end": v(0, -0.17) * mm});
            skLineSegment(sketch, "E729", {"start": v(0, -0.17) * mm, "end": v(0.04, -0.14) * mm});
            skLineSegment(sketch, "E730", {"start": v(0.04, -0.14) * mm, "end": v(0.08, -0.1) * mm});
            skLineSegment(sketch, "E731", {"start": v(1.06, -1.2) * mm, "end": v(1, -1.13) * mm});
            skLineSegment(sketch, "E732", {"start": v(1, -1.13) * mm, "end": v(0.95, -1.04) * mm});
            skLineSegment(sketch, "E733", {"start": v(0.95, -1.04) * mm, "end": v(0.92, -0.93) * mm});
            skLineSegment(sketch, "E734", {"start": v(0.92, -0.93) * mm, "end": v(0.91, -0.79) * mm});
            skLineSegment(sketch, "E735", {"start": v(0.91, -0.79) * mm, "end": v(0.91, -0.7) * mm});
            skLineSegment(sketch, "E736", {"start": v(0.91, -0.7) * mm, "end": v(0.92, -0.61) * mm});
            skLineSegment(sketch, "E737", {"start": v(0.92, -0.61) * mm, "end": v(0.94, -0.5) * mm});
            skLineSegment(sketch, "E738", {"start": v(0.94, -0.5) * mm, "end": v(0.97, -0.39) * mm});
            skLineSegment(sketch, "E739", {"start": v(0.97, -0.39) * mm, "end": v(1.01, -0.25) * mm});
            skLineSegment(sketch, "E740", {"start": v(1.01, -0.25) * mm, "end": v(1.07, -0.08) * mm});
            skLineSegment(sketch, "E741", {"start": v(1.07, -0.08) * mm, "end": v(1.13, 0.1) * mm});
            skLineSegment(sketch, "E742", {"start": v(1.13, 0.1) * mm, "end": v(1.21, 0.33) * mm});
            skLineSegment(sketch, "E743", {"start": v(1.21, 0.33) * mm, "end": v(1.25, 0.44) * mm});
            skLineSegment(sketch, "E744", {"start": v(1.25, 0.44) * mm, "end": v(1.29, 0.54) * mm});
            skLineSegment(sketch, "E745", {"start": v(1.29, 0.54) * mm, "end": v(1.32, 0.64) * mm});
            skLineSegment(sketch, "E746", {"start": v(1.32, 0.64) * mm, "end": v(1.35, 0.73) * mm});
            skLineSegment(sketch, "E747", {"start": v(1.35, 0.73) * mm, "end": v(1.38, 0.8) * mm});
            skLineSegment(sketch, "E748", {"start": v(1.38, 0.8) * mm, "end": v(1.4, 0.88) * mm});
            skLineSegment(sketch, "E749", {"start": v(1.4, 0.88) * mm, "end": v(1.41, 0.93) * mm});
            skLineSegment(sketch, "E750", {"start": v(1.41, 0.93) * mm, "end": v(1.42, 0.96) * mm});
            skLineSegment(sketch, "E751", {"start": v(1.42, 0.96) * mm, "end": v(1.43, 1) * mm});
            skLineSegment(sketch, "E752", {"start": v(1.43, 1) * mm, "end": v(1.43, 1.04) * mm});
            skLineSegment(sketch, "E753", {"start": v(1.43, 1.04) * mm, "end": v(1.42, 1.08) * mm});
            skLineSegment(sketch, "E754", {"start": v(1.42, 1.08) * mm, "end": v(1.4, 1.11) * mm});
            skLineSegment(sketch, "E755", {"start": v(1.4, 1.11) * mm, "end": v(1.4, 1.14) * mm});
            skLineSegment(sketch, "E756", {"start": v(1.4, 1.14) * mm, "end": v(1.37, 1.16) * mm});
            skLineSegment(sketch, "E757", {"start": v(1.37, 1.16) * mm, "end": v(1.35, 1.17) * mm});
            skLineSegment(sketch, "E758", {"start": v(1.35, 1.17) * mm, "end": v(1.32, 1.17) * mm});
            skLineSegment(sketch, "E759", {"start": v(1.32, 1.17) * mm, "end": v(1.25, 1.14) * mm});
            skLineSegment(sketch, "E760", {"start": v(1.25, 1.14) * mm, "end": v(1.17, 1.05) * mm});
            skLineSegment(sketch, "E761", {"start": v(1.17, 1.05) * mm, "end": v(1.09, 0.92) * mm});
            skLineSegment(sketch, "E762", {"start": v(1.09, 0.92) * mm, "end": v(1.02, 0.77) * mm});
            skLineSegment(sketch, "E763", {"start": v(1.02, 0.77) * mm, "end": v(0.95, 0.6) * mm});
            skLineSegment(sketch, "E764", {"start": v(0.95, 0.6) * mm, "end": v(0.91, 0.7) * mm});
            skLineSegment(sketch, "E765", {"start": v(0.91, 0.7) * mm, "end": v(0.89, 0.8) * mm});
            skLineSegment(sketch, "E766", {"start": v(0.89, 0.8) * mm, "end": v(0.9, 0.89) * mm});
            skLineSegment(sketch, "E767", {"start": v(0.9, 0.89) * mm, "end": v(0.94, 1) * mm});
            skLineSegment(sketch, "E768", {"start": v(0.94, 1) * mm, "end": v(1.02, 1.13) * mm});
            skLineSegment(sketch, "E769", {"start": v(1.02, 1.13) * mm, "end": v(1.1, 1.24) * mm});
            skLineSegment(sketch, "E770", {"start": v(1.1, 1.24) * mm, "end": v(1.18, 1.32) * mm});
            skLineSegment(sketch, "E771", {"start": v(1.18, 1.32) * mm, "end": v(1.27, 1.38) * mm});
            skLineSegment(sketch, "E772", {"start": v(1.27, 1.38) * mm, "end": v(1.36, 1.42) * mm});
            skLineSegment(sketch, "E773", {"start": v(1.36, 1.42) * mm, "end": v(1.45, 1.44) * mm});
            skLineSegment(sketch, "E774", {"start": v(1.45, 1.44) * mm, "end": v(1.53, 1.43) * mm});
            skLineSegment(sketch, "E775", {"start": v(1.53, 1.43) * mm, "end": v(1.6, 1.39) * mm});
            skLineSegment(sketch, "E776", {"start": v(1.6, 1.39) * mm, "end": v(1.67, 1.33) * mm});
            skLineSegment(sketch, "E777", {"start": v(1.67, 1.33) * mm, "end": v(1.72, 1.27) * mm});
            skLineSegment(sketch, "E778", {"start": v(1.72, 1.27) * mm, "end": v(1.75, 1.2) * mm});
            skLineSegment(sketch, "E779", {"start": v(1.75, 1.2) * mm, "end": v(1.77, 1.13) * mm});
            skLineSegment(sketch, "E780", {"start": v(1.77, 1.13) * mm, "end": v(1.77, 1.04) * mm});
            skLineSegment(sketch, "E781", {"start": v(1.77, 1.04) * mm, "end": v(1.76, 0.94) * mm});
            skLineSegment(sketch, "E782", {"start": v(1.76, 0.94) * mm, "end": v(1.73, 0.81) * mm});
            skLineSegment(sketch, "E783", {"start": v(1.73, 0.81) * mm, "end": v(1.69, 0.67) * mm});
            skLineSegment(sketch, "E784", {"start": v(1.69, 0.67) * mm, "end": v(1.63, 0.5) * mm});
            skLineSegment(sketch, "E785", {"start": v(1.63, 0.5) * mm, "end": v(1.57, 0.31) * mm});
            skLineSegment(sketch, "E786", {"start": v(1.57, 0.31) * mm, "end": v(1.5, 0.11) * mm});
            skLineSegment(sketch, "E787", {"start": v(1.5, 0.11) * mm, "end": v(1.44, -0.09) * mm});
            skLineSegment(sketch, "E788", {"start": v(1.44, -0.09) * mm, "end": v(1.38, -0.25) * mm});
            skLineSegment(sketch, "E789", {"start": v(1.38, -0.25) * mm, "end": v(1.33, -0.4) * mm});
            skLineSegment(sketch, "E790", {"start": v(1.33, -0.4) * mm, "end": v(1.29, -0.54) * mm});
            skLineSegment(sketch, "E791", {"start": v(1.29, -0.54) * mm, "end": v(1.26, -0.65) * mm});
            skLineSegment(sketch, "E792", {"start": v(1.26, -0.65) * mm, "end": v(1.25, -0.74) * mm});
            skLineSegment(sketch, "E793", {"start": v(1.25, -0.74) * mm, "end": v(1.24, -0.81) * mm});
            skLineSegment(sketch, "E794", {"start": v(1.24, -0.81) * mm, "end": v(1.24, -0.87) * mm});
            skLineSegment(sketch, "E795", {"start": v(1.24, -0.87) * mm, "end": v(1.26, -0.92) * mm});
            skLineSegment(sketch, "E796", {"start": v(1.26, -0.92) * mm, "end": v(1.29, -0.96) * mm});
            skLineSegment(sketch, "E797", {"start": v(1.29, -0.96) * mm, "end": v(1.32, -0.99) * mm});
            skLineSegment(sketch, "E798", {"start": v(1.32, -0.99) * mm, "end": v(1.35, -1) * mm});
            skLineSegment(sketch, "E799", {"start": v(1.35, -1) * mm, "end": v(1.38, -1.01) * mm});
            skLineSegment(sketch, "E800", {"start": v(1.38, -1.01) * mm, "end": v(1.42, -1) * mm});
            skLineSegment(sketch, "E801", {"start": v(1.42, -1) * mm, "end": v(1.5, -0.96) * mm});
            skLineSegment(sketch, "E802", {"start": v(1.5, -0.96) * mm, "end": v(1.57, -0.9) * mm});
            skLineSegment(sketch, "E803", {"start": v(1.57, -0.9) * mm, "end": v(1.65, -0.8) * mm});
            skLineSegment(sketch, "E804", {"start": v(1.65, -0.8) * mm, "end": v(1.73, -0.67) * mm});
            skLineSegment(sketch, "E805", {"start": v(1.73, -0.67) * mm, "end": v(1.8, -0.53) * mm});
            skLineSegment(sketch, "E806", {"start": v(1.8, -0.53) * mm, "end": v(1.88, -0.38) * mm});
            skLineSegment(sketch, "E807", {"start": v(1.88, -0.38) * mm, "end": v(1.94, -0.21) * mm});
            skLineSegment(sketch, "E808", {"start": v(1.94, -0.21) * mm, "end": v(2, -0.05) * mm});
            skLineSegment(sketch, "E809", {"start": v(2, -0.05) * mm, "end": v(2.03, 0.17) * mm});
            skLineSegment(sketch, "E810", {"start": v(2.03, 0.17) * mm, "end": v(2.05, 0.41) * mm});
            skLineSegment(sketch, "E811", {"start": v(2.05, 0.41) * mm, "end": v(2.05, 0.66) * mm});
            skLineSegment(sketch, "E812", {"start": v(2.05, 0.66) * mm, "end": v(2.02, 0.86) * mm});
            skLineSegment(sketch, "E813", {"start": v(2.02, 0.86) * mm, "end": v(2, 0.93) * mm});
            skLineSegment(sketch, "E814", {"start": v(2, 0.93) * mm, "end": v(2, 0.99) * mm});
            skLineSegment(sketch, "E815", {"start": v(2, 0.99) * mm, "end": v(2, 1.04) * mm});
            skLineSegment(sketch, "E816", {"start": v(2, 1.04) * mm, "end": v(2, 1.08) * mm});
            skLineSegment(sketch, "E817", {"start": v(2, 1.08) * mm, "end": v(2.02, 1.1) * mm});
            skLineSegment(sketch, "E818", {"start": v(2.02, 1.1) * mm, "end": v(2.05, 1.15) * mm});
            skLineSegment(sketch, "E819", {"start": v(2.05, 1.15) * mm, "end": v(2.1, 1.18) * mm});
            skLineSegment(sketch, "E820", {"start": v(2.1, 1.18) * mm, "end": v(2.14, 1.21) * mm});
            skLineSegment(sketch, "E821", {"start": v(2.14, 1.21) * mm, "end": v(2.19, 1.24) * mm});
            skLineSegment(sketch, "E822", {"start": v(2.19, 1.24) * mm, "end": v(2.23, 1.26) * mm});
            skLineSegment(sketch, "E823", {"start": v(2.23, 1.26) * mm, "end": v(2.26, 1.27) * mm});
            skLineSegment(sketch, "E824", {"start": v(2.26, 1.27) * mm, "end": v(2.29, 1.26) * mm});
            skLineSegment(sketch, "E825", {"start": v(2.29, 1.26) * mm, "end": v(2.3, 1.23) * mm});
            skLineSegment(sketch, "E826", {"start": v(2.3, 1.23) * mm, "end": v(2.31, 1.17) * mm});
            skLineSegment(sketch, "E827", {"start": v(2.31, 1.17) * mm, "end": v(2.32, 1.09) * mm});
            skLineSegment(sketch, "E828", {"start": v(2.32, 1.09) * mm, "end": v(2.33, 1) * mm});
            skLineSegment(sketch, "E829", {"start": v(2.33, 1) * mm, "end": v(2.33, 0.8) * mm});
            skLineSegment(sketch, "E830", {"start": v(2.33, 0.8) * mm, "end": v(2.3, 0.56) * mm});
            skLineSegment(sketch, "E831", {"start": v(2.3, 0.56) * mm, "end": v(2.25, 0.3) * mm});
            skLineSegment(sketch, "E832", {"start": v(2.25, 0.3) * mm, "end": v(2.18, 0.04) * mm});
            skLineSegment(sketch, "E833", {"start": v(2.18, 0.04) * mm, "end": v(2.09, -0.22) * mm});
            skLineSegment(sketch, "E834", {"start": v(2.09, -0.22) * mm, "end": v(1.99, -0.47) * mm});
            skLineSegment(sketch, "E835", {"start": v(1.99, -0.47) * mm, "end": v(1.87, -0.7) * mm});
            skLineSegment(sketch, "E836", {"start": v(1.87, -0.7) * mm, "end": v(1.75, -0.88) * mm});
            skLineSegment(sketch, "E837", {"start": v(1.75, -0.88) * mm, "end": v(1.68, -0.98) * mm});
            skLineSegment(sketch, "E838", {"start": v(1.68, -0.98) * mm, "end": v(1.6, -1.07) * mm});
            skLineSegment(sketch, "E839", {"start": v(1.6, -1.07) * mm, "end": v(1.53, -1.14) * mm});
            skLineSegment(sketch, "E840", {"start": v(1.53, -1.14) * mm, "end": v(1.48, -1.19) * mm});
            skLineSegment(sketch, "E841", {"start": v(1.48, -1.19) * mm, "end": v(1.38, -1.23) * mm});
            skLineSegment(sketch, "E842", {"start": v(1.38, -1.23) * mm, "end": v(1.26, -1.24) * mm});
            skLineSegment(sketch, "E843", {"start": v(1.26, -1.24) * mm, "end": v(1.15, -1.23) * mm});
            skLineSegment(sketch, "E844", {"start": v(1.15, -1.23) * mm, "end": v(1.06, -1.2) * mm});
            skLineSegment(sketch, "E845", {"start": v(2.19, -1.17) * mm, "end": v(2.14, -1.1) * mm});
            skLineSegment(sketch, "E846", {"start": v(2.14, -1.1) * mm, "end": v(2.1, -1.03) * mm});
            skLineSegment(sketch, "E847", {"start": v(2.1, -1.03) * mm, "end": v(2.1, -0.94) * mm});
            skLineSegment(sketch, "E848", {"start": v(2.1, -0.94) * mm, "end": v(2.1, -0.83) * mm});
            skLineSegment(sketch, "E849", {"start": v(2.1, -0.83) * mm, "end": v(2.12, -0.7) * mm});
            skLineSegment(sketch, "E850", {"start": v(2.12, -0.7) * mm, "end": v(2.15, -0.55) * mm});
            skLineSegment(sketch, "E851", {"start": v(2.15, -0.55) * mm, "end": v(2.2, -0.37) * mm});
            skLineSegment(sketch, "E852", {"start": v(2.2, -0.37) * mm, "end": v(2.28, -0.17) * mm});
            skLineSegment(sketch, "E853", {"start": v(2.28, -0.17) * mm, "end": v(2.35, -0.01) * mm});
            skLineSegment(sketch, "E854", {"start": v(2.35, -0.01) * mm, "end": v(2.4, 0.13) * mm});
            skLineSegment(sketch, "E855", {"start": v(2.4, 0.13) * mm, "end": v(2.46, 0.23) * mm});
            skLineSegment(sketch, "E856", {"start": v(2.46, 0.23) * mm, "end": v(2.49, 0.3) * mm});
            skLineSegment(sketch, "E857", {"start": v(2.49, 0.3) * mm, "end": v(2.52, 0.33) * mm});
            skLineSegment(sketch, "E858", {"start": v(2.52, 0.33) * mm, "end": v(2.55, 0.34) * mm});
            skLineSegment(sketch, "E859", {"start": v(2.55, 0.34) * mm, "end": v(2.56, 0.33) * mm});
            skLineSegment(sketch, "E860", {"start": v(2.56, 0.33) * mm, "end": v(2.59, 0.29) * mm});
            skLineSegment(sketch, "E861", {"start": v(2.59, 0.29) * mm, "end": v(2.61, 0.24) * mm});
            skLineSegment(sketch, "E862", {"start": v(2.61, 0.24) * mm, "end": v(2.62, 0.18) * mm});
            skLineSegment(sketch, "E863", {"start": v(2.62, 0.18) * mm, "end": v(2.63, 0.12) * mm});
            skLineSegment(sketch, "E864", {"start": v(2.63, 0.12) * mm, "end": v(2.62, 0.05) * mm});
            skLineSegment(sketch, "E865", {"start": v(2.62, 0.05) * mm, "end": v(2.6, -0.04) * mm});
            skLineSegment(sketch, "E866", {"start": v(2.6, -0.04) * mm, "end": v(2.57, -0.15) * mm});
            skLineSegment(sketch, "E867", {"start": v(2.57, -0.15) * mm, "end": v(2.53, -0.27) * mm});
            skLineSegment(sketch, "E868", {"start": v(2.53, -0.27) * mm, "end": v(2.48, -0.41) * mm});
            skLineSegment(sketch, "E869", {"start": v(2.48, -0.41) * mm, "end": v(2.43, -0.58) * mm});
            skLineSegment(sketch, "E870", {"start": v(2.43, -0.58) * mm, "end": v(2.38, -0.71) * mm});
            skLineSegment(sketch, "E871", {"start": v(2.38, -0.71) * mm, "end": v(2.35, -0.82) * mm});
            skLineSegment(sketch, "E872", {"start": v(2.35, -0.82) * mm, "end": v(2.33, -0.91) * mm});
            skLineSegment(sketch, "E873", {"start": v(2.33, -0.91) * mm, "end": v(2.32, -0.98) * mm});
            skLineSegment(sketch, "E874", {"start": v(2.32, -0.98) * mm, "end": v(2.32, -1.03) * mm});
            skLineSegment(sketch, "E875", {"start": v(2.32, -1.03) * mm, "end": v(2.33, -1.06) * mm});
            skLineSegment(sketch, "E876", {"start": v(2.33, -1.06) * mm, "end": v(2.35, -1.08) * mm});
            skLineSegment(sketch, "E877", {"start": v(2.35, -1.08) * mm, "end": v(2.42, -1.09) * mm});
            skLineSegment(sketch, "E878", {"start": v(2.42, -1.09) * mm, "end": v(2.49, -1.04) * mm});
            skLineSegment(sketch, "E879", {"start": v(2.49, -1.04) * mm, "end": v(2.57, -0.95) * mm});
            skLineSegment(sketch, "E880", {"start": v(2.57, -0.95) * mm, "end": v(2.67, -0.8) * mm});
            skLineSegment(sketch, "E881", {"start": v(2.67, -0.8) * mm, "end": v(2.76, -0.65) * mm});
            skLineSegment(sketch, "E882", {"start": v(2.76, -0.65) * mm, "end": v(2.84, -0.48) * mm});
            skLineSegment(sketch, "E883", {"start": v(2.84, -0.48) * mm, "end": v(2.91, -0.31) * mm});
            skLineSegment(sketch, "E884", {"start": v(2.91, -0.31) * mm, "end": v(2.97, -0.15) * mm});
            skLineSegment(sketch, "E885", {"start": v(2.97, -0.15) * mm, "end": v(3.02, 0) * mm});
            skLineSegment(sketch, "E886", {"start": v(3.02, 0) * mm, "end": v(3.05, 0.13) * mm});
            skLineSegment(sketch, "E887", {"start": v(3.05, 0.13) * mm, "end": v(3.05, 0.22) * mm});
            skLineSegment(sketch, "E888", {"start": v(3.05, 0.22) * mm, "end": v(3.04, 0.28) * mm});
            skLineSegment(sketch, "E889", {"start": v(3.04, 0.28) * mm, "end": v(3.02, 0.32) * mm});
            skLineSegment(sketch, "E890", {"start": v(3.02, 0.32) * mm, "end": v(3.01, 0.38) * mm});
            skLineSegment(sketch, "E891", {"start": v(3.01, 0.38) * mm, "end": v(3.01, 0.45) * mm});
            skLineSegment(sketch, "E892", {"start": v(3.01, 0.45) * mm, "end": v(3.02, 0.51) * mm});
            skLineSegment(sketch, "E893", {"start": v(3.02, 0.51) * mm, "end": v(3.04, 0.58) * mm});
            skLineSegment(sketch, "E894", {"start": v(3.04, 0.58) * mm, "end": v(3.06, 0.63) * mm});
            skLineSegment(sketch, "E895", {"start": v(3.06, 0.63) * mm, "end": v(3.1, 0.67) * mm});
            skLineSegment(sketch, "E896", {"start": v(3.1, 0.67) * mm, "end": v(3.12, 0.68) * mm});
            skLineSegment(sketch, "E897", {"start": v(3.12, 0.68) * mm, "end": v(3.15, 0.67) * mm});
            skLineSegment(sketch, "E898", {"start": v(3.15, 0.67) * mm, "end": v(3.2, 0.64) * mm});
            skLineSegment(sketch, "E899", {"start": v(3.2, 0.64) * mm, "end": v(3.25, 0.59) * mm});
            skLineSegment(sketch, "E900", {"start": v(3.25, 0.59) * mm, "end": v(3.3, 0.53) * mm});
            skLineSegment(sketch, "E901", {"start": v(3.3, 0.53) * mm, "end": v(3.41, 0.4) * mm});
            skLineSegment(sketch, "E902", {"start": v(3.41, 0.4) * mm, "end": v(3.53, 0.31) * mm});
            skLineSegment(sketch, "E903", {"start": v(3.53, 0.31) * mm, "end": v(3.63, 0.25) * mm});
            skLineSegment(sketch, "E904", {"start": v(3.63, 0.25) * mm, "end": v(3.7, 0.23) * mm});
            skLineSegment(sketch, "E905", {"start": v(3.7, 0.23) * mm, "end": v(3.73, 0.23) * mm});
            skLineSegment(sketch, "E906", {"start": v(3.73, 0.23) * mm, "end": v(3.75, 0.21) * mm});
            skLineSegment(sketch, "E907", {"start": v(3.75, 0.21) * mm, "end": v(3.76, 0.2) * mm});
            skLineSegment(sketch, "E908", {"start": v(3.76, 0.2) * mm, "end": v(3.77, 0.18) * mm});
            skLineSegment(sketch, "E909", {"start": v(3.77, 0.18) * mm, "end": v(3.75, 0.14) * mm});
            skLineSegment(sketch, "E910", {"start": v(3.75, 0.14) * mm, "end": v(3.7, 0.05) * mm});
            skLineSegment(sketch, "E911", {"start": v(3.7, 0.05) * mm, "end": v(3.64, -0.07) * mm});
            skLineSegment(sketch, "E912", {"start": v(3.64, -0.07) * mm, "end": v(3.57, -0.21) * mm});
            skLineSegment(sketch, "E913", {"start": v(3.57, -0.21) * mm, "end": v(3.43, -0.47) * mm});
            skLineSegment(sketch, "E914", {"start": v(3.43, -0.47) * mm, "end": v(3.33, -0.69) * mm});
            skLineSegment(sketch, "E915", {"start": v(3.33, -0.69) * mm, "end": v(3.28, -0.86) * mm});
            skLineSegment(sketch, "E916", {"start": v(3.28, -0.86) * mm, "end": v(3.28, -1) * mm});
            skLineSegment(sketch, "E917", {"start": v(3.28, -1) * mm, "end": v(3.3, -1.04) * mm});
            skLineSegment(sketch, "E918", {"start": v(3.3, -1.04) * mm, "end": v(3.3, -1.07) * mm});
            skLineSegment(sketch, "E919", {"start": v(3.3, -1.07) * mm, "end": v(3.33, -1.1) * mm});
            skLineSegment(sketch, "E920", {"start": v(3.33, -1.1) * mm, "end": v(3.35, -1.1) * mm});
            skLineSegment(sketch, "E921", {"start": v(3.35, -1.1) * mm, "end": v(3.37, -1.1) * mm});
            skLineSegment(sketch, "E922", {"start": v(3.37, -1.1) * mm, "end": v(3.4, -1.1) * mm});
            skLineSegment(sketch, "E923", {"start": v(3.4, -1.1) * mm, "end": v(3.44, -1.08) * mm});
            skLineSegment(sketch, "E924", {"start": v(3.44, -1.08) * mm, "end": v(3.48, -1.05) * mm});
            skLineSegment(sketch, "E925", {"start": v(3.48, -1.05) * mm, "end": v(3.58, -0.93) * mm});
            skLineSegment(sketch, "E926", {"start": v(3.58, -0.93) * mm, "end": v(3.67, -0.8) * mm});
            skLineSegment(sketch, "E927", {"start": v(3.67, -0.8) * mm, "end": v(3.73, -0.65) * mm});
            skLineSegment(sketch, "E928", {"start": v(3.73, -0.65) * mm, "end": v(3.78, -0.48) * mm});
            skLineSegment(sketch, "E929", {"start": v(3.78, -0.48) * mm, "end": v(3.82, -0.3) * mm});
            skLineSegment(sketch, "E930", {"start": v(3.82, -0.3) * mm, "end": v(3.88, -0.16) * mm});
            skLineSegment(sketch, "E931", {"start": v(3.88, -0.16) * mm, "end": v(3.95, -0.02) * mm});
            skLineSegment(sketch, "E932", {"start": v(3.95, -0.02) * mm, "end": v(4.03, 0.1) * mm});
            skLineSegment(sketch, "E933", {"start": v(4.03, 0.1) * mm, "end": v(4.11, 0.2) * mm});
            skLineSegment(sketch, "E934", {"start": v(4.11, 0.2) * mm, "end": v(4.2, 0.29) * mm});
            skLineSegment(sketch, "E935", {"start": v(4.2, 0.29) * mm, "end": v(4.3, 0.34) * mm});
            skLineSegment(sketch, "E936", {"start": v(4.3, 0.34) * mm, "end": v(4.4, 0.37) * mm});
            skLineSegment(sketch, "E937", {"start": v(4.4, 0.37) * mm, "end": v(4.5, 0.37) * mm});
            skLineSegment(sketch, "E938", {"start": v(4.5, 0.37) * mm, "end": v(4.57, 0.33) * mm});
            skLineSegment(sketch, "E939", {"start": v(4.57, 0.33) * mm, "end": v(4.61, 0.26) * mm});
            skLineSegment(sketch, "E940", {"start": v(4.61, 0.26) * mm, "end": v(4.62, 0.14) * mm});
            skLineSegment(sketch, "E941", {"start": v(4.62, 0.14) * mm, "end": v(4.58, -0.07) * mm});
            skLineSegment(sketch, "E942", {"start": v(4.58, -0.07) * mm, "end": v(4.5, -0.27) * mm});
            skLineSegment(sketch, "E943", {"start": v(4.5, -0.27) * mm, "end": v(4.35, -0.44) * mm});
            skLineSegment(sketch, "E944", {"start": v(4.35, -0.44) * mm, "end": v(4.15, -0.6) * mm});
            skLineSegment(sketch, "E945", {"start": v(4.15, -0.6) * mm, "end": v(4.07, -0.65) * mm});
            skLineSegment(sketch, "E946", {"start": v(4.07, -0.65) * mm, "end": v(4.02, -0.7) * mm});
            skLineSegment(sketch, "E947", {"start": v(4.02, -0.7) * mm, "end": v(4, -0.75) * mm});
            skLineSegment(sketch, "E948", {"start": v(4, -0.75) * mm, "end": v(4, -0.82) * mm});
            skLineSegment(sketch, "E949", {"start": v(4, -0.82) * mm, "end": v(4.01, -0.92) * mm});
            skLineSegment(sketch, "E950", {"start": v(4.01, -0.92) * mm, "end": v(4.05, -1.01) * mm});
            skLineSegment(sketch, "E951", {"start": v(4.05, -1.01) * mm, "end": v(4.11, -1.07) * mm});
            skLineSegment(sketch, "E952", {"start": v(4.11, -1.07) * mm, "end": v(4.18, -1.1) * mm});
            skLineSegment(sketch, "E953", {"start": v(4.18, -1.1) * mm, "end": v(4.28, -1.07) * mm});
            skLineSegment(sketch, "E954", {"start": v(4.28, -1.07) * mm, "end": v(4.4, -1) * mm});
            skLineSegment(sketch, "E955", {"start": v(4.4, -1) * mm, "end": v(4.5, -0.9) * mm});
            skLineSegment(sketch, "E956", {"start": v(4.5, -0.9) * mm, "end": v(4.6, -0.77) * mm});
            skLineSegment(sketch, "E957", {"start": v(4.6, -0.77) * mm, "end": v(4.62, -0.71) * mm});
            skLineSegment(sketch, "E958", {"start": v(4.62, -0.71) * mm, "end": v(4.65, -0.67) * mm});
            skLineSegment(sketch, "E959", {"start": v(4.65, -0.67) * mm, "end": v(4.67, -0.64) * mm});
            skLineSegment(sketch, "E960", {"start": v(4.67, -0.64) * mm, "end": v(4.7, -0.63) * mm});
            skLineSegment(sketch, "E961", {"start": v(4.7, -0.63) * mm, "end": v(4.7, -0.64) * mm});
            skLineSegment(sketch, "E962", {"start": v(4.7, -0.64) * mm, "end": v(4.72, -0.65) * mm});
            skLineSegment(sketch, "E963", {"start": v(4.72, -0.65) * mm, "end": v(4.73, -0.69) * mm});
            skLineSegment(sketch, "E964", {"start": v(4.73, -0.69) * mm, "end": v(4.73, -0.73) * mm});
            skLineSegment(sketch, "E965", {"start": v(4.73, -0.73) * mm, "end": v(4.71, -0.82) * mm});
            skLineSegment(sketch, "E966", {"start": v(4.71, -0.82) * mm, "end": v(4.67, -0.91) * mm});
            skLineSegment(sketch, "E967", {"start": v(4.67, -0.91) * mm, "end": v(4.6, -1) * mm});
            skLineSegment(sketch, "E968", {"start": v(4.6, -1) * mm, "end": v(4.53, -1.08) * mm});
            skLineSegment(sketch, "E969", {"start": v(4.53, -1.08) * mm, "end": v(4.43, -1.14) * mm});
            skLineSegment(sketch, "E970", {"start": v(4.43, -1.14) * mm, "end": v(4.33, -1.2) * mm});
            skLineSegment(sketch, "E971", {"start": v(4.33, -1.2) * mm, "end": v(4.23, -1.23) * mm});
            skLineSegment(sketch, "E972", {"start": v(4.23, -1.23) * mm, "end": v(4.13, -1.25) * mm});
            skLineSegment(sketch, "E973", {"start": v(4.13, -1.25) * mm, "end": v(4.05, -1.24) * mm});
            skLineSegment(sketch, "E974", {"start": v(4.05, -1.24) * mm, "end": v(3.99, -1.23) * mm});
            skLineSegment(sketch, "E975", {"start": v(3.99, -1.23) * mm, "end": v(3.94, -1.2) * mm});
            skLineSegment(sketch, "E976", {"start": v(3.94, -1.2) * mm, "end": v(3.89, -1.15) * mm});
            skLineSegment(sketch, "E977", {"start": v(3.89, -1.15) * mm, "end": v(3.85, -1.1) * mm});
            skLineSegment(sketch, "E978", {"start": v(3.85, -1.1) * mm, "end": v(3.82, -1.06) * mm});
            skLineSegment(sketch, "E979", {"start": v(3.82, -1.06) * mm, "end": v(3.8, -1.02) * mm});
            skLineSegment(sketch, "E980", {"start": v(3.8, -1.02) * mm, "end": v(3.78, -0.98) * mm});
            skLineSegment(sketch, "E981", {"start": v(3.78, -0.98) * mm, "end": v(3.77, -0.96) * mm});
            skLineSegment(sketch, "E982", {"start": v(3.77, -0.96) * mm, "end": v(3.77, -0.95) * mm});
            skLineSegment(sketch, "E983", {"start": v(3.77, -0.95) * mm, "end": v(3.76, -0.95) * mm});
            skLineSegment(sketch, "E984", {"start": v(3.76, -0.95) * mm, "end": v(3.75, -0.95) * mm});
            skLineSegment(sketch, "E985", {"start": v(3.75, -0.95) * mm, "end": v(3.73, -0.96) * mm});
            skLineSegment(sketch, "E986", {"start": v(3.73, -0.96) * mm, "end": v(3.71, -0.99) * mm});
            skLineSegment(sketch, "E987", {"start": v(3.71, -0.99) * mm, "end": v(3.69, -1.02) * mm});
            skLineSegment(sketch, "E988", {"start": v(3.69, -1.02) * mm, "end": v(3.65, -1.07) * mm});
            skLineSegment(sketch, "E989", {"start": v(3.65, -1.07) * mm, "end": v(3.6, -1.14) * mm});
            skLineSegment(sketch, "E990", {"start": v(3.6, -1.14) * mm, "end": v(3.54, -1.2) * mm});
            skLineSegment(sketch, "E991", {"start": v(3.54, -1.2) * mm, "end": v(3.48, -1.22) * mm});
            skLineSegment(sketch, "E992", {"start": v(3.48, -1.22) * mm, "end": v(3.4, -1.24) * mm});
            skLineSegment(sketch, "E993", {"start": v(3.4, -1.24) * mm, "end": v(3.27, -1.23) * mm});
            skLineSegment(sketch, "E994", {"start": v(3.27, -1.23) * mm, "end": v(3.17, -1.17) * mm});
            skLineSegment(sketch, "E995", {"start": v(3.17, -1.17) * mm, "end": v(3.1, -1.07) * mm});
            skLineSegment(sketch, "E996", {"start": v(3.1, -1.07) * mm, "end": v(3.08, -0.92) * mm});
            skLineSegment(sketch, "E997", {"start": v(3.08, -0.92) * mm, "end": v(3.07, -0.76) * mm});
            skLineSegment(sketch, "E998", {"start": v(3.07, -0.76) * mm, "end": v(3.1, -0.6) * mm});
            skLineSegment(sketch, "E999", {"start": v(3.1, -0.6) * mm, "end": v(3.17, -0.43) * mm});
            skLineSegment(sketch, "E1000", {"start": v(3.17, -0.43) * mm, "end": v(3.28, -0.21) * mm});
            skLineSegment(sketch, "E1001", {"start": v(3.28, -0.21) * mm, "end": v(3.44, 0.07) * mm});
            skLineSegment(sketch, "E1002", {"start": v(3.44, 0.07) * mm, "end": v(3.33, 0.11) * mm});
            skLineSegment(sketch, "E1003", {"start": v(3.33, 0.11) * mm, "end": v(3.28, 0.13) * mm});
            skLineSegment(sketch, "E1004", {"start": v(3.28, 0.13) * mm, "end": v(3.25, 0.14) * mm});
            skLineSegment(sketch, "E1005", {"start": v(3.25, 0.14) * mm, "end": v(3.22, 0.15) * mm});
            skLineSegment(sketch, "E1006", {"start": v(3.22, 0.15) * mm, "end": v(3.2, 0.14) * mm});
            skLineSegment(sketch, "E1007", {"start": v(3.2, 0.14) * mm, "end": v(3.19, 0.13) * mm});
            skLineSegment(sketch, "E1008", {"start": v(3.19, 0.13) * mm, "end": v(3.18, 0.1) * mm});
            skLineSegment(sketch, "E1009", {"start": v(3.18, 0.1) * mm, "end": v(3.17, 0.06) * mm});
            skLineSegment(sketch, "E1010", {"start": v(3.17, 0.06) * mm, "end": v(3.15, 0.01) * mm});
            skLineSegment(sketch, "E1011", {"start": v(3.15, 0.01) * mm, "end": v(3.13, -0.08) * mm});
            skLineSegment(sketch, "E1012", {"start": v(3.13, -0.08) * mm, "end": v(3.1, -0.19) * mm});
            skLineSegment(sketch, "E1013", {"start": v(3.1, -0.19) * mm, "end": v(3.05, -0.3) * mm});
            skLineSegment(sketch, "E1014", {"start": v(3.05, -0.3) * mm, "end": v(3, -0.42) * mm});
            skLineSegment(sketch, "E1015", {"start": v(3, -0.42) * mm, "end": v(2.96, -0.54) * mm});
            skLineSegment(sketch, "E1016", {"start": v(2.96, -0.54) * mm, "end": v(2.9, -0.66) * mm});
            skLineSegment(sketch, "E1017", {"start": v(2.9, -0.66) * mm, "end": v(2.86, -0.76) * mm});
            skLineSegment(sketch, "E1018", {"start": v(2.86, -0.76) * mm, "end": v(2.81, -0.84) * mm});
            skLineSegment(sketch, "E1019", {"start": v(2.81, -0.84) * mm, "end": v(2.73, -0.97) * mm});
            skLineSegment(sketch, "E1020", {"start": v(2.73, -0.97) * mm, "end": v(2.65, -1.08) * mm});
            skLineSegment(sketch, "E1021", {"start": v(2.65, -1.08) * mm, "end": v(2.57, -1.16) * mm});
            skLineSegment(sketch, "E1022", {"start": v(2.57, -1.16) * mm, "end": v(2.48, -1.21) * mm});
            skLineSegment(sketch, "E1023", {"start": v(2.48, -1.21) * mm, "end": v(2.4, -1.24) * mm});
            skLineSegment(sketch, "E1024", {"start": v(2.4, -1.24) * mm, "end": v(2.33, -1.25) * mm});
            skLineSegment(sketch, "E1025", {"start": v(2.33, -1.25) * mm, "end": v(2.25, -1.22) * mm});
            skLineSegment(sketch, "E1026", {"start": v(2.25, -1.22) * mm, "end": v(2.19, -1.17) * mm});
            skLineSegment(sketch, "E1027", {"start": v(4.24, -0.36) * mm, "end": v(4.28, -0.32) * mm});
            skLineSegment(sketch, "E1028", {"start": v(4.28, -0.32) * mm, "end": v(4.32, -0.27) * mm});
            skLineSegment(sketch, "E1029", {"start": v(4.32, -0.27) * mm, "end": v(4.35, -0.2) * mm});
            skLineSegment(sketch, "E1030", {"start": v(4.35, -0.2) * mm, "end": v(4.39, -0.14) * mm});
            skLineSegment(sketch, "E1031", {"start": v(4.39, -0.14) * mm, "end": v(4.42, -0.07) * mm});
            skLineSegment(sketch, "E1032", {"start": v(4.42, -0.07) * mm, "end": v(4.44, 0) * mm});
            skLineSegment(sketch, "E1033", {"start": v(4.44, 0) * mm, "end": v(4.46, 0.05) * mm});
            skLineSegment(sketch, "E1034", {"start": v(4.46, 0.05) * mm, "end": v(4.47, 0.1) * mm});
            skLineSegment(sketch, "E1035", {"start": v(4.47, 0.1) * mm, "end": v(4.46, 0.14) * mm});
            skLineSegment(sketch, "E1036", {"start": v(4.46, 0.14) * mm, "end": v(4.43, 0.15) * mm});
            skLineSegment(sketch, "E1037", {"start": v(4.43, 0.15) * mm, "end": v(4.39, 0.14) * mm});
            skLineSegment(sketch, "E1038", {"start": v(4.39, 0.14) * mm, "end": v(4.34, 0.1) * mm});
            skLineSegment(sketch, "E1039", {"start": v(4.34, 0.1) * mm, "end": v(4.28, 0.04) * mm});
            skLineSegment(sketch, "E1040", {"start": v(4.28, 0.04) * mm, "end": v(4.22, -0.04) * mm});
            skLineSegment(sketch, "E1041", {"start": v(4.22, -0.04) * mm, "end": v(4.17, -0.13) * mm});
            skLineSegment(sketch, "E1042", {"start": v(4.17, -0.13) * mm, "end": v(4.11, -0.24) * mm});
            skLineSegment(sketch, "E1043", {"start": v(4.11, -0.24) * mm, "end": v(4.07, -0.34) * mm});
            skLineSegment(sketch, "E1044", {"start": v(4.07, -0.34) * mm, "end": v(4.04, -0.42) * mm});
            skLineSegment(sketch, "E1045", {"start": v(4.04, -0.42) * mm, "end": v(4.03, -0.47) * mm});
            skLineSegment(sketch, "E1046", {"start": v(4.03, -0.47) * mm, "end": v(4.04, -0.5) * mm});
            skLineSegment(sketch, "E1047", {"start": v(4.04, -0.5) * mm, "end": v(4.06, -0.5) * mm});
            skLineSegment(sketch, "E1048", {"start": v(4.06, -0.5) * mm, "end": v(4.1, -0.48) * mm});
            skLineSegment(sketch, "E1049", {"start": v(4.1, -0.48) * mm, "end": v(4.16, -0.43) * mm});
            skLineSegment(sketch, "E1050", {"start": v(4.16, -0.43) * mm, "end": v(4.24, -0.36) * mm});
            skLineSegment(sketch, "E1051", {"start": v(2.67, 0.58) * mm, "end": v(2.66, 0.7) * mm});
            skLineSegment(sketch, "E1052", {"start": v(2.66, 0.7) * mm, "end": v(2.65, 0.8) * mm});
            skLineSegment(sketch, "E1053", {"start": v(2.65, 0.8) * mm, "end": v(2.65, 0.86) * mm});
            skLineSegment(sketch, "E1054", {"start": v(2.65, 0.86) * mm, "end": v(2.65, 0.91) * mm});
            skLineSegment(sketch, "E1055", {"start": v(2.65, 0.91) * mm, "end": v(2.66, 0.95) * mm});
            skLineSegment(sketch, "E1056", {"start": v(2.66, 0.95) * mm, "end": v(2.68, 0.98) * mm});
            skLineSegment(sketch, "E1057", {"start": v(2.68, 0.98) * mm, "end": v(2.7, 1) * mm});
            skLineSegment(sketch, "E1058", {"start": v(2.7, 1) * mm, "end": v(2.74, 1.03) * mm});
            skLineSegment(sketch, "E1059", {"start": v(2.74, 1.03) * mm, "end": v(2.78, 1.06) * mm});
            skLineSegment(sketch, "E1060", {"start": v(2.78, 1.06) * mm, "end": v(2.81, 1.08) * mm});
            skLineSegment(sketch, "E1061", {"start": v(2.81, 1.08) * mm, "end": v(2.84, 1.09) * mm});
            skLineSegment(sketch, "E1062", {"start": v(2.84, 1.09) * mm, "end": v(2.85, 1.09) * mm});
            skLineSegment(sketch, "E1063", {"start": v(2.85, 1.09) * mm, "end": v(2.86, 1.07) * mm});
            skLineSegment(sketch, "E1064", {"start": v(2.86, 1.07) * mm, "end": v(2.87, 1.03) * mm});
            skLineSegment(sketch, "E1065", {"start": v(2.87, 1.03) * mm, "end": v(2.88, 0.98) * mm});
            skLineSegment(sketch, "E1066", {"start": v(2.88, 0.98) * mm, "end": v(2.88, 0.91) * mm});
            skLineSegment(sketch, "E1067", {"start": v(2.88, 0.91) * mm, "end": v(2.89, 0.83) * mm});
            skLineSegment(sketch, "E1068", {"start": v(2.89, 0.83) * mm, "end": v(2.88, 0.76) * mm});
            skLineSegment(sketch, "E1069", {"start": v(2.88, 0.76) * mm, "end": v(2.86, 0.68) * mm});
            skLineSegment(sketch, "E1070", {"start": v(2.86, 0.68) * mm, "end": v(2.82, 0.6) * mm});
            skLineSegment(sketch, "E1071", {"start": v(2.82, 0.6) * mm, "end": v(2.8, 0.52) * mm});
            skLineSegment(sketch, "E1072", {"start": v(2.8, 0.52) * mm, "end": v(2.76, 0.47) * mm});
            skLineSegment(sketch, "E1073", {"start": v(2.76, 0.47) * mm, "end": v(2.74, 0.42) * mm});
            skLineSegment(sketch, "E1074", {"start": v(2.74, 0.42) * mm, "end": v(2.72, 0.4) * mm});
            skLineSegment(sketch, "E1075", {"start": v(2.72, 0.4) * mm, "end": v(2.7, 0.4) * mm});
            skLineSegment(sketch, "E1076", {"start": v(2.7, 0.4) * mm, "end": v(2.7, 0.45) * mm});
            skLineSegment(sketch, "E1077", {"start": v(2.7, 0.45) * mm, "end": v(2.68, 0.5) * mm});
            skLineSegment(sketch, "E1078", {"start": v(2.68, 0.5) * mm, "end": v(2.67, 0.58) * mm});
            skSolve(sketch);
        }
        {
            var Q0;
            Q0 = qSketchRegion(id + "F0", true);
            extrude(context, id + "F2", {"entities" : qUnion([Q0]), "oppositeDirection" : true, "depth" : 5 * mm});
        }
        {
            var Q0;
            Q0=makeQuery(id+"F1.imprint","IMPRINT",FACE,{"disambiguationData":[TD([[makeQuery(id+"F1.imprint","IMPRINT",EDGE,{"derivedFrom":sQuery(id+"F1.wireOp",EDGE,"E107")}),1.0]])]});
            var Q1;
            Q1=makeQuery(id+"F1.imprint","IMPRINT",FACE,{"disambiguationData":[TD([[makeQuery(id+"F1.imprint","IMPRINT",EDGE,{"derivedFrom":sQuery(id+"F1.wireOp",EDGE,"E531")}),1.0]])]});
            var Q2;
            Q2=makeQuery(id+"F1.imprint","IMPRINT",FACE,{"disambiguationData":[TD([[makeQuery(id+"F1.imprint","IMPRINT",EDGE,{"derivedFrom":sQuery(id+"F1.wireOp",EDGE,"E563")}),1.0]])]});
            var Q3;
            Q3=makeQuery(id+"F1.imprint","IMPRINT",FACE,{"disambiguationData":[TD([[makeQuery(id+"F1.imprint","IMPRINT",EDGE,{"derivedFrom":sQuery(id+"F1.wireOp",EDGE,"E507")}),1.0]])]});
            var Q4;
            Q4=makeQuery(id+"F1.imprint","IMPRINT",FACE,{"disambiguationData":[TD([[makeQuery(id+"F1.imprint","IMPRINT",EDGE,{"derivedFrom":sQuery(id+"F1.wireOp",EDGE,"E711")}),1.0]])]});
            var Q5;
            Q5=makeQuery(id+"F1.imprint","IMPRINT",FACE,{"disambiguationData":[TD([[makeQuery(id+"F1.imprint","IMPRINT",EDGE,{"derivedFrom":sQuery(id+"F1.wireOp",EDGE,"E689")}),1.0]])]});
            var Q6;
            Q6=makeQuery(id+"F1.imprint","IMPRINT",FACE,{"disambiguationData":[TD([[makeQuery(id+"F1.imprint","IMPRINT",EDGE,{"derivedFrom":sQuery(id+"F1.wireOp",EDGE,"E1027")}),1.0]])]});
            extrude(context, id + "F3", {"entities" : qUnion([Q0, Q1, Q2, Q3, Q4, Q5, Q6]), "operationType" : NewBodyOperationType.ADD, "depth" : 0.5 * mm, "hasDraft" : true, "draftAngle" : 5 * degree, "draftPullDirection" : true});
        }
    });
